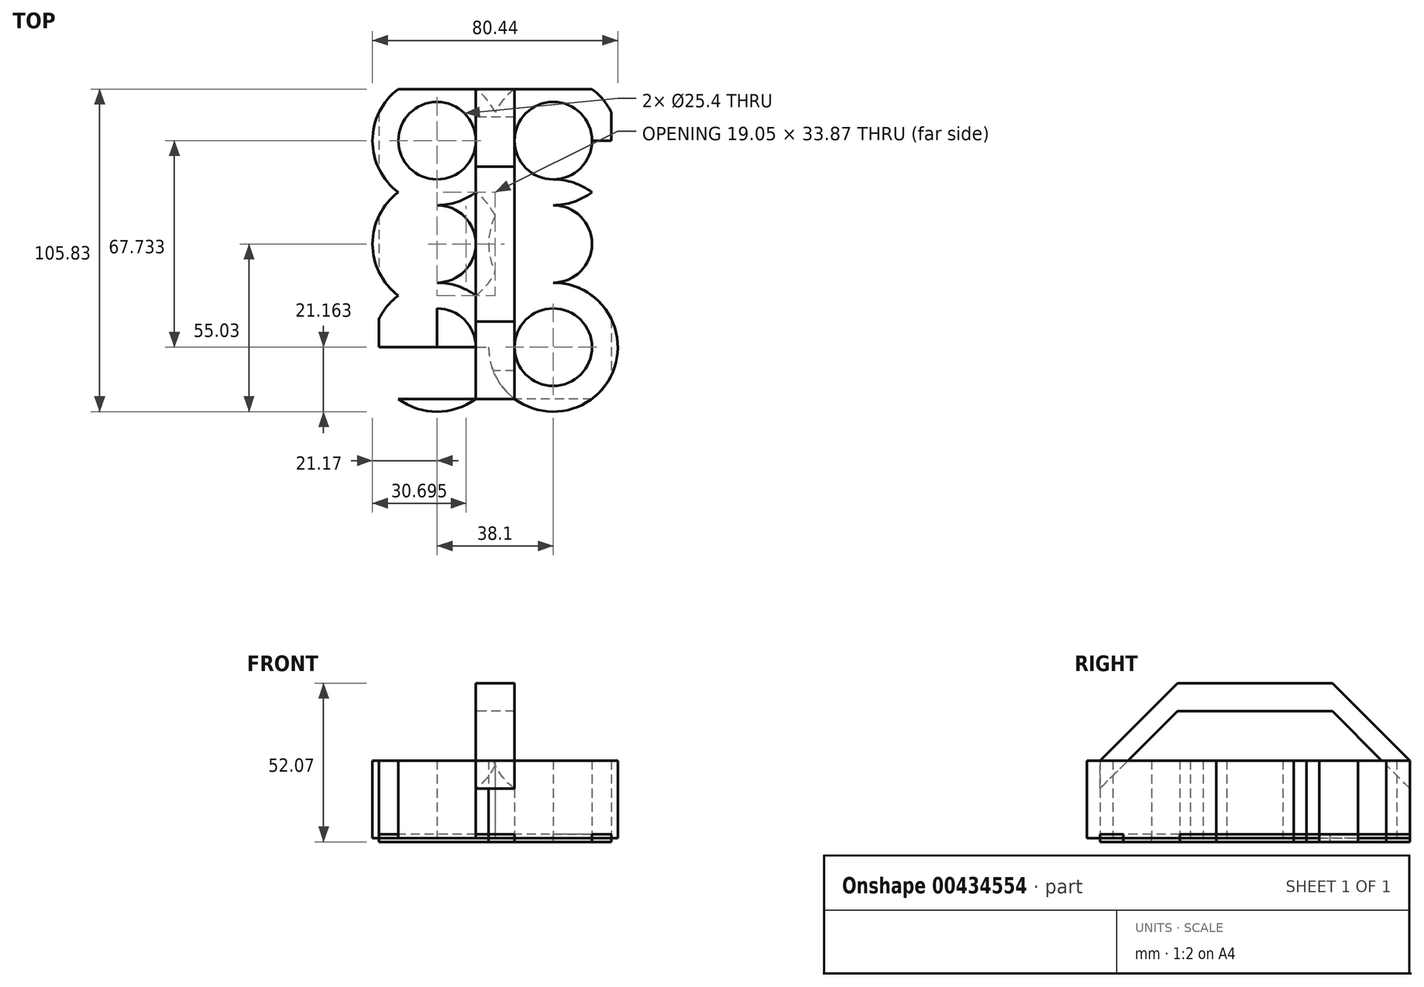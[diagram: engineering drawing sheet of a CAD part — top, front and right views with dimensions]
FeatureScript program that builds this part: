
annotation { "Feature Type Name" : "Feature", "Feature Type Description" : "" }
export const myFeature = defineFeature(function(context is Context, id is Id, definition is map)
    precondition{}
    {
        {
            var Q0;
            Q0=qCreatedBy(makeId("Top.planeOp"),FACE);
            var sketch = newSketch(context, id + "F0", { "sketchPlane" : qUnion([Q0])});
            skCircle(sketch, "E0", {"center": v(-19.05, 33.87) * mm, "radius": 12.7 * mm});
            skCircle(sketch, "E1", {"center": v(19.05, 33.87) * mm, "radius": 12.7 * mm});
            skCircle(sketch, "E2", {"center": v(-19.05, 0) * mm, "radius": 12.7 * mm});
            skCircle(sketch, "E3", {"center": v(19.05, 0) * mm, "radius": 12.7 * mm});
            skCircle(sketch, "E4", {"center": v(-19.05, -33.87) * mm, "radius": 12.7 * mm});
            skCircle(sketch, "E5", {"center": v(19.05, -33.87) * mm, "radius": 12.7 * mm});
            skLineSegment(sketch, "E6.bottom", {"start": v(38.1, 50.8) * mm, "end": v(-38.1, 50.8) * mm});
            skLineSegment(sketch, "E6.top", {"start": v(38.1, -50.8) * mm, "end": v(-38.1, -50.8) * mm});
            skLineSegment(sketch, "E6.left", {"start": v(38.1, 50.8) * mm, "end": v(38.1, -50.8) * mm});
            skLineSegment(sketch, "E6.right", {"start": v(-38.1, 50.8) * mm, "end": v(-38.1, -50.8) * mm});
            skPoint(sketch, "E6.middle", {"position": v(0, 0) * mm});
            skLineSegment(sketch, "E7", {"start": v(0, 50.8) * mm, "end": v(0, -50.8) * mm});
            skLineSegment(sketch, "E8", {"start": v(-38.1, 0) * mm, "end": v(38.1, 0) * mm});
            skLineSegment(sketch, "E9", {"start": v(0, 50.8) * mm, "end": v(-38.1, 50.8) * mm});
            skLineSegment(sketch, "E10", {"start": v(-19.05, 50.8) * mm, "end": v(-19.05, -50.8) * mm});
            skLineSegment(sketch, "E11", {"start": v(0, 50.8) * mm, "end": v(38.1, 50.8) * mm});
            skLineSegment(sketch, "E12", {"start": v(19.05, 50.8) * mm, "end": v(19.05, -50.8) * mm});
            skLineSegment(sketch, "E13", {"start": v(38.1, 50.8) * mm, "end": v(38.1, 16.93) * mm});
            skLineSegment(sketch, "E14", {"start": v(38.1, 16.93) * mm, "end": v(38.1, -16.93) * mm});
            skLineSegment(sketch, "E15", {"start": v(38.1, 16.93) * mm, "end": v(-38.1, 16.93) * mm});
            skLineSegment(sketch, "E16", {"start": v(38.1, -16.93) * mm, "end": v(-38.1, -16.93) * mm});
            skLineSegment(sketch, "E17", {"start": v(-38.1, -16.93) * mm, "end": v(-38.1, -50.8) * mm});
            skLineSegment(sketch, "E18", {"start": v(-38.1, -33.87) * mm, "end": v(38.1, -33.87) * mm});
            skLineSegment(sketch, "E19", {"start": v(38.1, 33.87) * mm, "end": v(-38.1, 33.87) * mm});
            skCircle(sketch, "E20", {"center": v(-19.05, 0) * mm, "radius": 21.17 * mm});
            skCircle(sketch, "E21", {"center": v(19.05, 0) * mm, "radius": 21.17 * mm});
            skCircle(sketch, "E22", {"center": v(-19.05, 33.87) * mm, "radius": 21.17 * mm});
            skCircle(sketch, "E23", {"center": v(19.05, 33.87) * mm, "radius": 21.17 * mm});
            skCircle(sketch, "E24", {"center": v(19.05, -33.87) * mm, "radius": 21.17 * mm});
            skCircle(sketch, "E25", {"center": v(-19.05, -33.87) * mm, "radius": 21.17 * mm});
            skSolve(sketch);
        }
        {
            var Q0;
            {var subQ1=sQuery(id+"F0.wireOp",EDGE,"E0");var subQ5=sQuery(id+"F0.wireOp",EDGE,"E10");var subQ10=makeQuery(id+"F0.imprint","INTERSECT",VERTEX,{"derivedFrom":[subQ1,subQ5]});Q0=makeQuery(id+"F0.imprint","IMPRINT",FACE,{"disambiguationData":[TD([[makeQuery(id+"F0.imprint","IMPRINT",EDGE,{"disambiguationData":[TD([[subQ10,1.0]])],"derivedFrom":subQ1}),-1.0]])]});}
            var Q1;
            {var subQ0=sQuery(id+"F0.wireOp",EDGE,"E9");var subQ1=makeQuery(id+"F0.imprint","INTERSECT",VERTEX,{"derivedFrom":[subQ0,sQuery(id+"F0.wireOp",EDGE,"E10")]});Q1=makeQuery(id+"F0.imprint","IMPRINT",FACE,{"disambiguationData":[TD([[makeQuery(id+"F0.imprint","IMPRINT",EDGE,{"disambiguationData":[TD([[subQ1,1.0]])],"derivedFrom":subQ0}),-1.0]])]});}
            var Q2;
            {var subQ0=sQuery(id+"F0.wireOp",EDGE,"E10");var subQ3=sQuery(id+"F0.wireOp",EDGE,"E0");var subQ4=makeQuery(id+"F0.imprint","INTERSECT",VERTEX,{"derivedFrom":[subQ3,subQ0]});Q2=makeQuery(id+"F0.imprint","IMPRINT",FACE,{"disambiguationData":[TD([[makeQuery(id+"F0.imprint","IMPRINT",EDGE,{"disambiguationData":[TD([[subQ4,-1.0]])],"derivedFrom":subQ3}),-1.0]])]});}
            var Q3;
            {var subQ0=sQuery(id+"F0.wireOp",EDGE,"E6.right");var subQ1=makeQuery(id+"F0.imprint","INTERSECT",VERTEX,{"derivedFrom":[subQ0,sQuery(id+"F0.wireOp",EDGE,"E19")]});Q3=makeQuery(id+"F0.imprint","IMPRINT",FACE,{"disambiguationData":[TD([[makeQuery(id+"F0.imprint","IMPRINT",EDGE,{"disambiguationData":[TD([[subQ1,1.0]])],"derivedFrom":subQ0}),-1.0]])]});}
            var Q4;
            {var subQ5=sQuery(id+"F0.wireOp",EDGE,"E19");var subQ6=sQuery(id+"F0.wireOp",EDGE,"E6.right");var subQ7=makeQuery(id+"F0.imprint","INTERSECT",VERTEX,{"derivedFrom":[subQ6,subQ5]});Q4=makeQuery(id+"F0.imprint","IMPRINT",FACE,{"disambiguationData":[TD([[makeQuery(id+"F0.imprint","IMPRINT",EDGE,{"disambiguationData":[TD([[subQ7,-1.0]])],"derivedFrom":subQ6}),1.0]])]});}
            var Q5;
            {var subQ0=sQuery(id+"F0.wireOp",EDGE,"E15");var subQ1=sQuery(id+"F0.wireOp",EDGE,"E10");var subQ2=makeQuery(id+"F0.imprint","INTERSECT",VERTEX,{"derivedFrom":[subQ1,subQ0]});Q5=makeQuery(id+"F0.imprint","IMPRINT",FACE,{"disambiguationData":[TD([[makeQuery(id+"F0.imprint","IMPRINT",EDGE,{"disambiguationData":[TD([[subQ2,-1.0]])],"derivedFrom":subQ1}),-1.0]])]});}
            var Q6;
            {var subQ0=sQuery(id+"F0.wireOp",EDGE,"E15");var subQ1=sQuery(id+"F0.wireOp",EDGE,"E10");var subQ2=makeQuery(id+"F0.imprint","INTERSECT",VERTEX,{"derivedFrom":[subQ1,subQ0]});Q6=makeQuery(id+"F0.imprint","IMPRINT",FACE,{"disambiguationData":[TD([[makeQuery(id+"F0.imprint","IMPRINT",EDGE,{"disambiguationData":[TD([[subQ2,1.0]])],"derivedFrom":subQ1}),-1.0]])]});}
            var Q7;
            {var subQ0=sQuery(id+"F0.wireOp",EDGE,"E15");var subQ1=sQuery(id+"F0.wireOp",EDGE,"E10");var subQ2=makeQuery(id+"F0.imprint","INTERSECT",VERTEX,{"derivedFrom":[subQ1,subQ0]});Q7=makeQuery(id+"F0.imprint","IMPRINT",FACE,{"disambiguationData":[TD([[makeQuery(id+"F0.imprint","IMPRINT",EDGE,{"disambiguationData":[TD([[subQ2,1.0]])],"derivedFrom":subQ1}),1.0]])]});}
            var Q8;
            {var subQ0=sQuery(id+"F0.wireOp",EDGE,"E15");var subQ1=sQuery(id+"F0.wireOp",EDGE,"E10");var subQ2=makeQuery(id+"F0.imprint","INTERSECT",VERTEX,{"derivedFrom":[subQ1,subQ0]});Q8=makeQuery(id+"F0.imprint","IMPRINT",FACE,{"disambiguationData":[TD([[makeQuery(id+"F0.imprint","IMPRINT",EDGE,{"disambiguationData":[TD([[subQ2,-1.0]])],"derivedFrom":subQ1}),1.0]])]});}
            var Q9;
            {var subQ5=sQuery(id+"F0.wireOp",EDGE,"E19");var subQ6=sQuery(id+"F0.wireOp",EDGE,"E0");var subQ7=makeQuery(id+"F0.imprint","INTERSECT",VERTEX,{"disambiguationData":[OD(0.0)],"derivedFrom":[subQ6,subQ5]});Q9=makeQuery(id+"F0.imprint","IMPRINT",FACE,{"disambiguationData":[TD([[makeQuery(id+"F0.imprint","IMPRINT",EDGE,{"disambiguationData":[TD([[subQ7,1.0]])],"derivedFrom":subQ5}),1.0]])]});}
            var Q10;
            {var subQ0=sQuery(id+"F0.wireOp",EDGE,"E19");var subQ1=sQuery(id+"F0.wireOp",EDGE,"E7");var subQ2=makeQuery(id+"F0.imprint","INTERSECT",VERTEX,{"derivedFrom":[subQ1,subQ0]});Q10=makeQuery(id+"F0.imprint","IMPRINT",FACE,{"disambiguationData":[TD([[makeQuery(id+"F0.imprint","IMPRINT",EDGE,{"disambiguationData":[TD([[subQ2,-1.0]])],"derivedFrom":subQ0}),1.0]])]});}
            var Q11;
            {var subQ0=sQuery(id+"F0.wireOp",EDGE,"E19");var subQ1=sQuery(id+"F0.wireOp",EDGE,"E7");var subQ2=makeQuery(id+"F0.imprint","INTERSECT",VERTEX,{"derivedFrom":[subQ1,subQ0]});Q11=makeQuery(id+"F0.imprint","IMPRINT",FACE,{"disambiguationData":[TD([[makeQuery(id+"F0.imprint","IMPRINT",EDGE,{"disambiguationData":[TD([[subQ2,1.0]])],"derivedFrom":subQ0}),1.0]])]});}
            var Q12;
            {var subQ0=sQuery(id+"F0.wireOp",EDGE,"E19");var subQ1=sQuery(id+"F0.wireOp",EDGE,"E7");var subQ2=makeQuery(id+"F0.imprint","INTERSECT",VERTEX,{"derivedFrom":[subQ1,subQ0]});Q12=makeQuery(id+"F0.imprint","IMPRINT",FACE,{"disambiguationData":[TD([[makeQuery(id+"F0.imprint","IMPRINT",EDGE,{"disambiguationData":[TD([[subQ2,1.0]])],"derivedFrom":subQ0}),-1.0]])]});}
            var Q13;
            {var subQ0=sQuery(id+"F0.wireOp",EDGE,"E19");var subQ1=sQuery(id+"F0.wireOp",EDGE,"E7");var subQ2=makeQuery(id+"F0.imprint","INTERSECT",VERTEX,{"derivedFrom":[subQ1,subQ0]});Q13=makeQuery(id+"F0.imprint","IMPRINT",FACE,{"disambiguationData":[TD([[makeQuery(id+"F0.imprint","IMPRINT",EDGE,{"disambiguationData":[TD([[subQ2,-1.0]])],"derivedFrom":subQ0}),-1.0]])]});}
            var Q14;
            {var subQ1=sQuery(id+"F0.wireOp",EDGE,"E1");var subQ5=sQuery(id+"F0.wireOp",EDGE,"E12");var subQ8=makeQuery(id+"F0.imprint","INTERSECT",VERTEX,{"derivedFrom":[subQ1,subQ5]});Q14=makeQuery(id+"F0.imprint","IMPRINT",FACE,{"disambiguationData":[TD([[makeQuery(id+"F0.imprint","IMPRINT",EDGE,{"disambiguationData":[TD([[subQ8,-1.0]])],"derivedFrom":subQ1}),-1.0]])]});}
            var Q15;
            {var subQ1=sQuery(id+"F0.wireOp",EDGE,"E19");var subQ6=sQuery(id+"F0.wireOp",EDGE,"E1");var subQ9=makeQuery(id+"F0.imprint","INTERSECT",VERTEX,{"disambiguationData":[OD(1.0)],"derivedFrom":[subQ6,subQ1]});Q15=makeQuery(id+"F0.imprint","IMPRINT",FACE,{"disambiguationData":[TD([[makeQuery(id+"F0.imprint","IMPRINT",EDGE,{"disambiguationData":[TD([[subQ9,-1.0]])],"derivedFrom":subQ1}),1.0]])]});}
            var Q16;
            {var subQ0=sQuery(id+"F0.wireOp",EDGE,"E15");var subQ1=sQuery(id+"F0.wireOp",EDGE,"E12");var subQ2=makeQuery(id+"F0.imprint","INTERSECT",VERTEX,{"derivedFrom":[subQ1,subQ0]});Q16=makeQuery(id+"F0.imprint","IMPRINT",FACE,{"disambiguationData":[TD([[makeQuery(id+"F0.imprint","IMPRINT",EDGE,{"disambiguationData":[TD([[subQ2,-1.0]])],"derivedFrom":subQ1}),-1.0]])]});}
            var Q17;
            {var subQ0=sQuery(id+"F0.wireOp",EDGE,"E15");var subQ1=sQuery(id+"F0.wireOp",EDGE,"E12");var subQ2=makeQuery(id+"F0.imprint","INTERSECT",VERTEX,{"derivedFrom":[subQ1,subQ0]});Q17=makeQuery(id+"F0.imprint","IMPRINT",FACE,{"disambiguationData":[TD([[makeQuery(id+"F0.imprint","IMPRINT",EDGE,{"disambiguationData":[TD([[subQ2,1.0]])],"derivedFrom":subQ1}),-1.0]])]});}
            var Q18;
            {var subQ0=sQuery(id+"F0.wireOp",EDGE,"E15");var subQ1=sQuery(id+"F0.wireOp",EDGE,"E12");var subQ2=makeQuery(id+"F0.imprint","INTERSECT",VERTEX,{"derivedFrom":[subQ1,subQ0]});Q18=makeQuery(id+"F0.imprint","IMPRINT",FACE,{"disambiguationData":[TD([[makeQuery(id+"F0.imprint","IMPRINT",EDGE,{"disambiguationData":[TD([[subQ2,-1.0]])],"derivedFrom":subQ1}),1.0]])]});}
            var Q19;
            {var subQ0=sQuery(id+"F0.wireOp",EDGE,"E15");var subQ1=sQuery(id+"F0.wireOp",EDGE,"E12");var subQ2=makeQuery(id+"F0.imprint","INTERSECT",VERTEX,{"derivedFrom":[subQ1,subQ0]});Q19=makeQuery(id+"F0.imprint","IMPRINT",FACE,{"disambiguationData":[TD([[makeQuery(id+"F0.imprint","IMPRINT",EDGE,{"disambiguationData":[TD([[subQ2,1.0]])],"derivedFrom":subQ1}),1.0]])]});}
            var Q20;
            {var subQ5=sQuery(id+"F0.wireOp",EDGE,"E19");var subQ6=sQuery(id+"F0.wireOp",EDGE,"E13");var subQ7=makeQuery(id+"F0.imprint","INTERSECT",VERTEX,{"derivedFrom":[subQ6,subQ5]});Q20=makeQuery(id+"F0.imprint","IMPRINT",FACE,{"disambiguationData":[TD([[makeQuery(id+"F0.imprint","IMPRINT",EDGE,{"disambiguationData":[TD([[subQ7,-1.0]])],"derivedFrom":subQ6}),-1.0]])]});}
            var Q21;
            {var subQ0=sQuery(id+"F0.wireOp",EDGE,"E12");var subQ3=sQuery(id+"F0.wireOp",EDGE,"E1");var subQ4=makeQuery(id+"F0.imprint","INTERSECT",VERTEX,{"derivedFrom":[subQ3,subQ0]});Q21=makeQuery(id+"F0.imprint","IMPRINT",FACE,{"disambiguationData":[TD([[makeQuery(id+"F0.imprint","IMPRINT",EDGE,{"disambiguationData":[TD([[subQ4,1.0]])],"derivedFrom":subQ3}),-1.0]])]});}
            var Q22;
            {var subQ0=sQuery(id+"F0.wireOp",EDGE,"E11");var subQ1=makeQuery(id+"F0.imprint","INTERSECT",VERTEX,{"derivedFrom":[subQ0,sQuery(id+"F0.wireOp",EDGE,"E12")]});Q22=makeQuery(id+"F0.imprint","IMPRINT",FACE,{"disambiguationData":[TD([[makeQuery(id+"F0.imprint","IMPRINT",EDGE,{"disambiguationData":[TD([[subQ1,1.0]])],"derivedFrom":subQ0}),1.0]])]});}
            var Q23;
            {var subQ0=sQuery(id+"F0.wireOp",EDGE,"E13");var subQ1=makeQuery(id+"F0.imprint","INTERSECT",VERTEX,{"derivedFrom":[subQ0,sQuery(id+"F0.wireOp",EDGE,"E19")]});Q23=makeQuery(id+"F0.imprint","IMPRINT",FACE,{"disambiguationData":[TD([[makeQuery(id+"F0.imprint","IMPRINT",EDGE,{"disambiguationData":[TD([[subQ1,1.0]])],"derivedFrom":subQ0}),1.0]])]});}
            var Q24;
            {var subQ0=sQuery(id+"F0.wireOp",EDGE,"E8");var subQ1=sQuery(id+"F0.wireOp",EDGE,"E7");var subQ2=makeQuery(id+"F0.imprint","INTERSECT",VERTEX,{"derivedFrom":[subQ1,subQ0]});Q24=makeQuery(id+"F0.imprint","IMPRINT",FACE,{"disambiguationData":[TD([[makeQuery(id+"F0.imprint","IMPRINT",EDGE,{"disambiguationData":[TD([[subQ2,-1.0]])],"derivedFrom":subQ0}),1.0]])]});}
            var Q25;
            {var subQ0=sQuery(id+"F0.wireOp",EDGE,"E8");var subQ1=sQuery(id+"F0.wireOp",EDGE,"E7");var subQ2=makeQuery(id+"F0.imprint","INTERSECT",VERTEX,{"derivedFrom":[subQ1,subQ0]});Q25=makeQuery(id+"F0.imprint","IMPRINT",FACE,{"disambiguationData":[TD([[makeQuery(id+"F0.imprint","IMPRINT",EDGE,{"disambiguationData":[TD([[subQ2,1.0]])],"derivedFrom":subQ0}),1.0]])]});}
            var Q26;
            {var subQ0=sQuery(id+"F0.wireOp",EDGE,"E8");var subQ1=sQuery(id+"F0.wireOp",EDGE,"E7");var subQ2=makeQuery(id+"F0.imprint","INTERSECT",VERTEX,{"derivedFrom":[subQ1,subQ0]});Q26=makeQuery(id+"F0.imprint","IMPRINT",FACE,{"disambiguationData":[TD([[makeQuery(id+"F0.imprint","IMPRINT",EDGE,{"disambiguationData":[TD([[subQ2,1.0]])],"derivedFrom":subQ0}),-1.0]])]});}
            var Q27;
            {var subQ0=sQuery(id+"F0.wireOp",EDGE,"E8");var subQ1=sQuery(id+"F0.wireOp",EDGE,"E7");var subQ2=makeQuery(id+"F0.imprint","INTERSECT",VERTEX,{"derivedFrom":[subQ1,subQ0]});Q27=makeQuery(id+"F0.imprint","IMPRINT",FACE,{"disambiguationData":[TD([[makeQuery(id+"F0.imprint","IMPRINT",EDGE,{"disambiguationData":[TD([[subQ2,-1.0]])],"derivedFrom":subQ0}),-1.0]])]});}
            var Q28;
            {var subQ1=sQuery(id+"F0.wireOp",EDGE,"E8");var subQ7=sQuery(id+"F0.wireOp",EDGE,"E2");var subQ8=makeQuery(id+"F0.imprint","INTERSECT",VERTEX,{"disambiguationData":[OD(0.0)],"derivedFrom":[subQ7,subQ1]});Q28=makeQuery(id+"F0.imprint","IMPRINT",FACE,{"disambiguationData":[TD([[makeQuery(id+"F0.imprint","IMPRINT",EDGE,{"disambiguationData":[TD([[subQ8,-1.0]])],"derivedFrom":subQ1}),1.0]])]});}
            var Q29;
            {var subQ1=sQuery(id+"F0.wireOp",EDGE,"E8");var subQ7=sQuery(id+"F0.wireOp",EDGE,"E2");var subQ8=makeQuery(id+"F0.imprint","INTERSECT",VERTEX,{"disambiguationData":[OD(0.0)],"derivedFrom":[subQ7,subQ1]});Q29=makeQuery(id+"F0.imprint","IMPRINT",FACE,{"disambiguationData":[TD([[makeQuery(id+"F0.imprint","IMPRINT",EDGE,{"disambiguationData":[TD([[subQ8,-1.0]])],"derivedFrom":subQ1}),-1.0]])]});}
            var Q30;
            {var subQ0=sQuery(id+"F0.wireOp",EDGE,"E16");var subQ1=sQuery(id+"F0.wireOp",EDGE,"E10");var subQ2=makeQuery(id+"F0.imprint","INTERSECT",VERTEX,{"derivedFrom":[subQ1,subQ0]});Q30=makeQuery(id+"F0.imprint","IMPRINT",FACE,{"disambiguationData":[TD([[makeQuery(id+"F0.imprint","IMPRINT",EDGE,{"disambiguationData":[TD([[subQ2,1.0]])],"derivedFrom":subQ1}),1.0]])]});}
            var Q31;
            {var subQ0=sQuery(id+"F0.wireOp",EDGE,"E16");var subQ1=sQuery(id+"F0.wireOp",EDGE,"E10");var subQ2=makeQuery(id+"F0.imprint","INTERSECT",VERTEX,{"derivedFrom":[subQ1,subQ0]});Q31=makeQuery(id+"F0.imprint","IMPRINT",FACE,{"disambiguationData":[TD([[makeQuery(id+"F0.imprint","IMPRINT",EDGE,{"disambiguationData":[TD([[subQ2,-1.0]])],"derivedFrom":subQ1}),1.0]])]});}
            var Q32;
            {var subQ0=sQuery(id+"F0.wireOp",EDGE,"E16");var subQ1=sQuery(id+"F0.wireOp",EDGE,"E10");var subQ2=makeQuery(id+"F0.imprint","INTERSECT",VERTEX,{"derivedFrom":[subQ1,subQ0]});Q32=makeQuery(id+"F0.imprint","IMPRINT",FACE,{"disambiguationData":[TD([[makeQuery(id+"F0.imprint","IMPRINT",EDGE,{"disambiguationData":[TD([[subQ2,-1.0]])],"derivedFrom":subQ1}),-1.0]])]});}
            var Q33;
            {var subQ0=sQuery(id+"F0.wireOp",EDGE,"E16");var subQ1=sQuery(id+"F0.wireOp",EDGE,"E10");var subQ2=makeQuery(id+"F0.imprint","INTERSECT",VERTEX,{"derivedFrom":[subQ1,subQ0]});Q33=makeQuery(id+"F0.imprint","IMPRINT",FACE,{"disambiguationData":[TD([[makeQuery(id+"F0.imprint","IMPRINT",EDGE,{"disambiguationData":[TD([[subQ2,1.0]])],"derivedFrom":subQ1}),-1.0]])]});}
            var Q34;
            {var subQ0=sQuery(id+"F0.wireOp",EDGE,"E8");var subQ1=sQuery(id+"F0.wireOp",EDGE,"E6.right");var subQ2=makeQuery(id+"F0.imprint","INTERSECT",VERTEX,{"derivedFrom":[subQ1,subQ0]});Q34=makeQuery(id+"F0.imprint","IMPRINT",FACE,{"disambiguationData":[TD([[makeQuery(id+"F0.imprint","IMPRINT",EDGE,{"disambiguationData":[TD([[subQ2,-1.0]])],"derivedFrom":subQ1}),1.0]])]});}
            var Q35;
            {var subQ0=sQuery(id+"F0.wireOp",EDGE,"E6.right");var subQ1=makeQuery(id+"F0.imprint","INTERSECT",VERTEX,{"derivedFrom":[subQ0,sQuery(id+"F0.wireOp",EDGE,"E8")]});Q35=makeQuery(id+"F0.imprint","IMPRINT",FACE,{"disambiguationData":[TD([[makeQuery(id+"F0.imprint","IMPRINT",EDGE,{"disambiguationData":[TD([[subQ1,1.0]])],"derivedFrom":subQ0}),-1.0]])]});}
            var Q36;
            {var subQ1=sQuery(id+"F0.wireOp",EDGE,"E6.right");var subQ5=sQuery(id+"F0.wireOp",EDGE,"E8");var subQ6=makeQuery(id+"F0.imprint","INTERSECT",VERTEX,{"derivedFrom":[subQ1,subQ5]});Q36=makeQuery(id+"F0.imprint","IMPRINT",FACE,{"disambiguationData":[TD([[makeQuery(id+"F0.imprint","IMPRINT",EDGE,{"disambiguationData":[TD([[subQ6,1.0]])],"derivedFrom":subQ1}),1.0]])]});}
            var Q37;
            {var subQ5=sQuery(id+"F0.wireOp",EDGE,"E8");var subQ7=sQuery(id+"F0.wireOp",EDGE,"E3");var subQ8=makeQuery(id+"F0.imprint","INTERSECT",VERTEX,{"disambiguationData":[OD(1.0)],"derivedFrom":[subQ7,subQ5]});Q37=makeQuery(id+"F0.imprint","IMPRINT",FACE,{"disambiguationData":[TD([[makeQuery(id+"F0.imprint","IMPRINT",EDGE,{"disambiguationData":[TD([[subQ8,1.0]])],"derivedFrom":subQ5}),1.0]])]});}
            var Q38;
            {var subQ0=sQuery(id+"F0.wireOp",EDGE,"E16");var subQ1=sQuery(id+"F0.wireOp",EDGE,"E12");var subQ2=makeQuery(id+"F0.imprint","INTERSECT",VERTEX,{"derivedFrom":[subQ1,subQ0]});Q38=makeQuery(id+"F0.imprint","IMPRINT",FACE,{"disambiguationData":[TD([[makeQuery(id+"F0.imprint","IMPRINT",EDGE,{"disambiguationData":[TD([[subQ2,1.0]])],"derivedFrom":subQ1}),-1.0]])]});}
            var Q39;
            {var subQ0=sQuery(id+"F0.wireOp",EDGE,"E16");var subQ1=sQuery(id+"F0.wireOp",EDGE,"E12");var subQ2=makeQuery(id+"F0.imprint","INTERSECT",VERTEX,{"derivedFrom":[subQ1,subQ0]});Q39=makeQuery(id+"F0.imprint","IMPRINT",FACE,{"disambiguationData":[TD([[makeQuery(id+"F0.imprint","IMPRINT",EDGE,{"disambiguationData":[TD([[subQ2,-1.0]])],"derivedFrom":subQ1}),-1.0]])]});}
            var Q40;
            {var subQ0=sQuery(id+"F0.wireOp",EDGE,"E16");var subQ1=sQuery(id+"F0.wireOp",EDGE,"E12");var subQ2=makeQuery(id+"F0.imprint","INTERSECT",VERTEX,{"derivedFrom":[subQ1,subQ0]});Q40=makeQuery(id+"F0.imprint","IMPRINT",FACE,{"disambiguationData":[TD([[makeQuery(id+"F0.imprint","IMPRINT",EDGE,{"disambiguationData":[TD([[subQ2,-1.0]])],"derivedFrom":subQ1}),1.0]])]});}
            var Q41;
            {var subQ0=sQuery(id+"F0.wireOp",EDGE,"E16");var subQ1=sQuery(id+"F0.wireOp",EDGE,"E12");var subQ2=makeQuery(id+"F0.imprint","INTERSECT",VERTEX,{"derivedFrom":[subQ1,subQ0]});Q41=makeQuery(id+"F0.imprint","IMPRINT",FACE,{"disambiguationData":[TD([[makeQuery(id+"F0.imprint","IMPRINT",EDGE,{"disambiguationData":[TD([[subQ2,1.0]])],"derivedFrom":subQ1}),1.0]])]});}
            var Q42;
            {var subQ1=sQuery(id+"F0.wireOp",EDGE,"E14");var subQ5=sQuery(id+"F0.wireOp",EDGE,"E8");var subQ6=makeQuery(id+"F0.imprint","INTERSECT",VERTEX,{"derivedFrom":[subQ5,subQ1]});Q42=makeQuery(id+"F0.imprint","IMPRINT",FACE,{"disambiguationData":[TD([[makeQuery(id+"F0.imprint","IMPRINT",EDGE,{"disambiguationData":[TD([[subQ6,1.0]])],"derivedFrom":subQ5}),-1.0]])]});}
            var Q43;
            {var subQ0=sQuery(id+"F0.wireOp",EDGE,"E14");var subQ1=sQuery(id+"F0.wireOp",EDGE,"E8");var subQ2=makeQuery(id+"F0.imprint","INTERSECT",VERTEX,{"derivedFrom":[subQ1,subQ0]});Q43=makeQuery(id+"F0.imprint","IMPRINT",FACE,{"disambiguationData":[TD([[makeQuery(id+"F0.imprint","IMPRINT",EDGE,{"disambiguationData":[TD([[subQ2,1.0]])],"derivedFrom":subQ1}),1.0]])]});}
            var Q44;
            {var subQ0=sQuery(id+"F0.wireOp",EDGE,"E14");var subQ1=makeQuery(id+"F0.imprint","INTERSECT",VERTEX,{"derivedFrom":[sQuery(id+"F0.wireOp",EDGE,"E8"),subQ0]});Q44=makeQuery(id+"F0.imprint","IMPRINT",FACE,{"disambiguationData":[TD([[makeQuery(id+"F0.imprint","IMPRINT",EDGE,{"disambiguationData":[TD([[subQ1,1.0]])],"derivedFrom":subQ0}),1.0]])]});}
            var Q45;
            {var subQ5=sQuery(id+"F0.wireOp",EDGE,"E8");var subQ7=sQuery(id+"F0.wireOp",EDGE,"E3");var subQ8=makeQuery(id+"F0.imprint","INTERSECT",VERTEX,{"disambiguationData":[OD(1.0)],"derivedFrom":[subQ7,subQ5]});Q45=makeQuery(id+"F0.imprint","IMPRINT",FACE,{"disambiguationData":[TD([[makeQuery(id+"F0.imprint","IMPRINT",EDGE,{"disambiguationData":[TD([[subQ8,1.0]])],"derivedFrom":subQ5}),-1.0]])]});}
            var Q46;
            {var subQ1=sQuery(id+"F0.wireOp",EDGE,"E5");var subQ5=sQuery(id+"F0.wireOp",EDGE,"E18");var subQ6=makeQuery(id+"F0.imprint","INTERSECT",VERTEX,{"disambiguationData":[OD(1.0)],"derivedFrom":[subQ1,subQ5]});Q46=makeQuery(id+"F0.imprint","IMPRINT",FACE,{"disambiguationData":[TD([[makeQuery(id+"F0.imprint","IMPRINT",EDGE,{"disambiguationData":[TD([[subQ6,1.0]])],"derivedFrom":subQ5}),1.0]])]});}
            var Q47;
            {var subQ0=sQuery(id+"F0.wireOp",EDGE,"E18");var subQ1=sQuery(id+"F0.wireOp",EDGE,"E7");var subQ2=makeQuery(id+"F0.imprint","INTERSECT",VERTEX,{"derivedFrom":[subQ1,subQ0]});Q47=makeQuery(id+"F0.imprint","IMPRINT",FACE,{"disambiguationData":[TD([[makeQuery(id+"F0.imprint","IMPRINT",EDGE,{"disambiguationData":[TD([[subQ2,-1.0]])],"derivedFrom":subQ0}),1.0]])]});}
            var Q48;
            {var subQ0=sQuery(id+"F0.wireOp",EDGE,"E18");var subQ1=sQuery(id+"F0.wireOp",EDGE,"E7");var subQ2=makeQuery(id+"F0.imprint","INTERSECT",VERTEX,{"derivedFrom":[subQ1,subQ0]});Q48=makeQuery(id+"F0.imprint","IMPRINT",FACE,{"disambiguationData":[TD([[makeQuery(id+"F0.imprint","IMPRINT",EDGE,{"disambiguationData":[TD([[subQ2,1.0]])],"derivedFrom":subQ0}),1.0]])]});}
            var Q49;
            {var subQ0=sQuery(id+"F0.wireOp",EDGE,"E18");var subQ1=sQuery(id+"F0.wireOp",EDGE,"E7");var subQ2=makeQuery(id+"F0.imprint","INTERSECT",VERTEX,{"derivedFrom":[subQ1,subQ0]});Q49=makeQuery(id+"F0.imprint","IMPRINT",FACE,{"disambiguationData":[TD([[makeQuery(id+"F0.imprint","IMPRINT",EDGE,{"disambiguationData":[TD([[subQ2,-1.0]])],"derivedFrom":subQ0}),-1.0]])]});}
            var Q50;
            {var subQ0=sQuery(id+"F0.wireOp",EDGE,"E18");var subQ1=sQuery(id+"F0.wireOp",EDGE,"E7");var subQ2=makeQuery(id+"F0.imprint","INTERSECT",VERTEX,{"derivedFrom":[subQ1,subQ0]});Q50=makeQuery(id+"F0.imprint","IMPRINT",FACE,{"disambiguationData":[TD([[makeQuery(id+"F0.imprint","IMPRINT",EDGE,{"disambiguationData":[TD([[subQ2,1.0]])],"derivedFrom":subQ0}),-1.0]])]});}
            var Q51;
            {var subQ5=sQuery(id+"F0.wireOp",EDGE,"E18");var subQ6=sQuery(id+"F0.wireOp",EDGE,"E5");var subQ7=makeQuery(id+"F0.imprint","INTERSECT",VERTEX,{"disambiguationData":[OD(1.0)],"derivedFrom":[subQ6,subQ5]});Q51=makeQuery(id+"F0.imprint","IMPRINT",FACE,{"disambiguationData":[TD([[makeQuery(id+"F0.imprint","IMPRINT",EDGE,{"disambiguationData":[TD([[subQ7,-1.0]])],"derivedFrom":subQ6}),-1.0]])]});}
            var Q52;
            {var subQ0=sQuery(id+"F0.wireOp",EDGE,"E6.top");var subQ1=makeQuery(id+"F0.imprint","INTERSECT",VERTEX,{"derivedFrom":[subQ0,sQuery(id+"F0.wireOp",EDGE,"E12")]});Q52=makeQuery(id+"F0.imprint","IMPRINT",FACE,{"disambiguationData":[TD([[makeQuery(id+"F0.imprint","IMPRINT",EDGE,{"disambiguationData":[TD([[subQ1,1.0]])],"derivedFrom":subQ0}),1.0]])]});}
            var Q53;
            {var subQ3=sQuery(id+"F0.wireOp",EDGE,"E5");var subQ9=sQuery(id+"F0.wireOp",EDGE,"E18");var subQ11=makeQuery(id+"F0.imprint","INTERSECT",VERTEX,{"disambiguationData":[OD(0.0)],"derivedFrom":[subQ3,subQ9]});Q53=makeQuery(id+"F0.imprint","IMPRINT",FACE,{"disambiguationData":[TD([[makeQuery(id+"F0.imprint","IMPRINT",EDGE,{"disambiguationData":[TD([[subQ11,1.0]])],"derivedFrom":subQ3}),-1.0]])]});}
            var Q54;
            {var subQ0=sQuery(id+"F0.wireOp",EDGE,"E18");var subQ1=sQuery(id+"F0.wireOp",EDGE,"E6.left");var subQ2=makeQuery(id+"F0.imprint","INTERSECT",VERTEX,{"derivedFrom":[subQ1,subQ0]});Q54=makeQuery(id+"F0.imprint","IMPRINT",FACE,{"disambiguationData":[TD([[makeQuery(id+"F0.imprint","IMPRINT",EDGE,{"disambiguationData":[TD([[subQ2,1.0]])],"derivedFrom":subQ1}),-1.0]])]});}
            var Q55;
            {var subQ0=sQuery(id+"F0.wireOp",EDGE,"E6.left");var subQ1=makeQuery(id+"F0.imprint","INTERSECT",VERTEX,{"derivedFrom":[subQ0,sQuery(id+"F0.wireOp",EDGE,"E18")]});Q55=makeQuery(id+"F0.imprint","IMPRINT",FACE,{"disambiguationData":[TD([[makeQuery(id+"F0.imprint","IMPRINT",EDGE,{"disambiguationData":[TD([[subQ1,1.0]])],"derivedFrom":subQ0}),1.0]])]});}
            var Q56;
            {var subQ1=sQuery(id+"F0.wireOp",EDGE,"E18");var subQ5=sQuery(id+"F0.wireOp",EDGE,"E4");var subQ6=makeQuery(id+"F0.imprint","INTERSECT",VERTEX,{"disambiguationData":[OD(0.0)],"derivedFrom":[subQ5,subQ1]});Q56=makeQuery(id+"F0.imprint","IMPRINT",FACE,{"disambiguationData":[TD([[makeQuery(id+"F0.imprint","IMPRINT",EDGE,{"disambiguationData":[TD([[subQ6,-1.0]])],"derivedFrom":subQ1}),1.0]])]});}
            var Q57;
            {var subQ0=sQuery(id+"F0.wireOp",EDGE,"E18");var subQ1=sQuery(id+"F0.wireOp",EDGE,"E17");var subQ2=makeQuery(id+"F0.imprint","INTERSECT",VERTEX,{"derivedFrom":[subQ1,subQ0]});Q57=makeQuery(id+"F0.imprint","IMPRINT",FACE,{"disambiguationData":[TD([[makeQuery(id+"F0.imprint","IMPRINT",EDGE,{"disambiguationData":[TD([[subQ2,1.0]])],"derivedFrom":subQ1}),1.0]])]});}
            var Q58;
            {var subQ0=sQuery(id+"F0.wireOp",EDGE,"E17");var subQ1=makeQuery(id+"F0.imprint","INTERSECT",VERTEX,{"derivedFrom":[subQ0,sQuery(id+"F0.wireOp",EDGE,"E18")]});Q58=makeQuery(id+"F0.imprint","IMPRINT",FACE,{"disambiguationData":[TD([[makeQuery(id+"F0.imprint","IMPRINT",EDGE,{"disambiguationData":[TD([[subQ1,1.0]])],"derivedFrom":subQ0}),-1.0]])]});}
            var Q59;
            {var subQ0=sQuery(id+"F0.wireOp",EDGE,"E18");var subQ8=sQuery(id+"F0.wireOp",EDGE,"E4");var subQ11=makeQuery(id+"F0.imprint","INTERSECT",VERTEX,{"disambiguationData":[OD(1.0)],"derivedFrom":[subQ8,subQ0]});Q59=makeQuery(id+"F0.imprint","IMPRINT",FACE,{"disambiguationData":[TD([[makeQuery(id+"F0.imprint","IMPRINT",EDGE,{"disambiguationData":[TD([[subQ11,-1.0]])],"derivedFrom":subQ8}),-1.0]])]});}
            var Q60;
            {var subQ0=sQuery(id+"F0.wireOp",EDGE,"E6.top");var subQ1=makeQuery(id+"F0.imprint","INTERSECT",VERTEX,{"derivedFrom":[subQ0,sQuery(id+"F0.wireOp",EDGE,"E10")]});Q60=makeQuery(id+"F0.imprint","IMPRINT",FACE,{"disambiguationData":[TD([[makeQuery(id+"F0.imprint","IMPRINT",EDGE,{"disambiguationData":[TD([[subQ1,1.0]])],"derivedFrom":subQ0}),1.0]])]});}
            var Q61;
            {var subQ3=sQuery(id+"F0.wireOp",EDGE,"E4");var subQ5=sQuery(id+"F0.wireOp",EDGE,"E18");var subQ6=makeQuery(id+"F0.imprint","INTERSECT",VERTEX,{"disambiguationData":[OD(0.0)],"derivedFrom":[subQ3,subQ5]});Q61=makeQuery(id+"F0.imprint","IMPRINT",FACE,{"disambiguationData":[TD([[makeQuery(id+"F0.imprint","IMPRINT",EDGE,{"disambiguationData":[TD([[subQ6,1.0]])],"derivedFrom":subQ3}),-1.0]])]});}
            var Q62;
            {var subQ0=sQuery(id+"F0.wireOp",EDGE,"E15");var subQ1=sQuery(id+"F0.wireOp",EDGE,"E7");var subQ2=makeQuery(id+"F0.imprint","INTERSECT",VERTEX,{"derivedFrom":[subQ1,subQ0]});Q62=makeQuery(id+"F0.imprint","IMPRINT",FACE,{"disambiguationData":[TD([[makeQuery(id+"F0.imprint","IMPRINT",EDGE,{"disambiguationData":[TD([[subQ2,-1.0]])],"derivedFrom":subQ1}),-1.0]])]});}
            var Q63;
            {var subQ0=sQuery(id+"F0.wireOp",EDGE,"E15");var subQ1=sQuery(id+"F0.wireOp",EDGE,"E7");var subQ2=makeQuery(id+"F0.imprint","INTERSECT",VERTEX,{"derivedFrom":[subQ1,subQ0]});Q63=makeQuery(id+"F0.imprint","IMPRINT",FACE,{"disambiguationData":[TD([[makeQuery(id+"F0.imprint","IMPRINT",EDGE,{"disambiguationData":[TD([[subQ2,-1.0]])],"derivedFrom":subQ1}),1.0]])]});}
            var Q64;
            {var subQ0=sQuery(id+"F0.wireOp",EDGE,"E15");var subQ1=sQuery(id+"F0.wireOp",EDGE,"E7");var subQ2=makeQuery(id+"F0.imprint","INTERSECT",VERTEX,{"derivedFrom":[subQ1,subQ0]});Q64=makeQuery(id+"F0.imprint","IMPRINT",FACE,{"disambiguationData":[TD([[makeQuery(id+"F0.imprint","IMPRINT",EDGE,{"disambiguationData":[TD([[subQ2,1.0]])],"derivedFrom":subQ1}),1.0]])]});}
            var Q65;
            {var subQ0=sQuery(id+"F0.wireOp",EDGE,"E15");var subQ1=sQuery(id+"F0.wireOp",EDGE,"E7");var subQ2=makeQuery(id+"F0.imprint","INTERSECT",VERTEX,{"derivedFrom":[subQ1,subQ0]});Q65=makeQuery(id+"F0.imprint","IMPRINT",FACE,{"disambiguationData":[TD([[makeQuery(id+"F0.imprint","IMPRINT",EDGE,{"disambiguationData":[TD([[subQ2,1.0]])],"derivedFrom":subQ1}),-1.0]])]});}
            var Q66;
            {var subQ0=sQuery(id+"F0.wireOp",EDGE,"E16");var subQ1=sQuery(id+"F0.wireOp",EDGE,"E7");var subQ2=makeQuery(id+"F0.imprint","INTERSECT",VERTEX,{"derivedFrom":[subQ1,subQ0]});Q66=makeQuery(id+"F0.imprint","IMPRINT",FACE,{"disambiguationData":[TD([[makeQuery(id+"F0.imprint","IMPRINT",EDGE,{"disambiguationData":[TD([[subQ2,1.0]])],"derivedFrom":subQ1}),-1.0]])]});}
            var Q67;
            {var subQ0=sQuery(id+"F0.wireOp",EDGE,"E16");var subQ1=sQuery(id+"F0.wireOp",EDGE,"E7");var subQ2=makeQuery(id+"F0.imprint","INTERSECT",VERTEX,{"derivedFrom":[subQ1,subQ0]});Q67=makeQuery(id+"F0.imprint","IMPRINT",FACE,{"disambiguationData":[TD([[makeQuery(id+"F0.imprint","IMPRINT",EDGE,{"disambiguationData":[TD([[subQ2,1.0]])],"derivedFrom":subQ1}),1.0]])]});}
            var Q68;
            {var subQ0=sQuery(id+"F0.wireOp",EDGE,"E16");var subQ1=sQuery(id+"F0.wireOp",EDGE,"E7");var subQ2=makeQuery(id+"F0.imprint","INTERSECT",VERTEX,{"derivedFrom":[subQ1,subQ0]});Q68=makeQuery(id+"F0.imprint","IMPRINT",FACE,{"disambiguationData":[TD([[makeQuery(id+"F0.imprint","IMPRINT",EDGE,{"disambiguationData":[TD([[subQ2,-1.0]])],"derivedFrom":subQ1}),1.0]])]});}
            var Q69;
            {var subQ0=sQuery(id+"F0.wireOp",EDGE,"E16");var subQ1=sQuery(id+"F0.wireOp",EDGE,"E7");var subQ2=makeQuery(id+"F0.imprint","INTERSECT",VERTEX,{"derivedFrom":[subQ1,subQ0]});Q69=makeQuery(id+"F0.imprint","IMPRINT",FACE,{"disambiguationData":[TD([[makeQuery(id+"F0.imprint","IMPRINT",EDGE,{"disambiguationData":[TD([[subQ2,-1.0]])],"derivedFrom":subQ1}),-1.0]])]});}
            extrude(context, id + "F1", {"entities" : qUnion([Q0, Q1, Q2, Q3, Q4, Q5, Q6, Q7, Q8, Q9, Q10, Q11, Q12, Q13, Q14, Q15, Q16, Q17, Q18, Q19, Q20, Q21, Q22, Q23, Q24, Q25, Q26, Q27, Q28, Q29, Q30, Q31, Q32, Q33, Q34, Q35, Q36, Q37, Q38, Q39, Q40, Q41, Q42, Q43, Q44, Q45, Q46, Q47, Q48, Q49, Q50, Q51, Q52, Q53, Q54, Q55, Q56, Q57, Q58, Q59, Q60, Q61, Q62, Q63, Q64, Q65, Q66, Q67, Q68, Q69]), "depth" : 25.4 * mm});
        }
        {
            var Q0;
            {var subQ0=sQuery(id+"F0.wireOp",EDGE,"E10");var subQ1=sQuery(id+"F0.wireOp",EDGE,"E0");var subQ2=makeQuery(id+"F0.imprint","INTERSECT",VERTEX,{"derivedFrom":[subQ1,subQ0]});Q0=makeQuery(id+"F0.imprint","IMPRINT",FACE,{"disambiguationData":[TD([[makeQuery(id+"F0.imprint","IMPRINT",EDGE,{"disambiguationData":[TD([[subQ2,-1.0]])],"derivedFrom":subQ1}),1.0]])]});}
            var Q1;
            {var subQ0=sQuery(id+"F0.wireOp",EDGE,"E10");var subQ1=sQuery(id+"F0.wireOp",EDGE,"E0");var subQ2=makeQuery(id+"F0.imprint","INTERSECT",VERTEX,{"derivedFrom":[subQ1,subQ0]});Q1=makeQuery(id+"F0.imprint","IMPRINT",FACE,{"disambiguationData":[TD([[makeQuery(id+"F0.imprint","IMPRINT",EDGE,{"disambiguationData":[TD([[subQ2,1.0]])],"derivedFrom":subQ1}),1.0]])]});}
            var Q2;
            {var subQ0=sQuery(id+"F0.wireOp",EDGE,"E19");var subQ1=sQuery(id+"F0.wireOp",EDGE,"E0");var subQ2=makeQuery(id+"F0.imprint","INTERSECT",VERTEX,{"disambiguationData":[OD(1.0)],"derivedFrom":[subQ1,subQ0]});Q2=makeQuery(id+"F0.imprint","IMPRINT",FACE,{"disambiguationData":[TD([[makeQuery(id+"F0.imprint","IMPRINT",EDGE,{"disambiguationData":[TD([[subQ2,1.0]])],"derivedFrom":subQ0}),1.0]])]});}
            var Q3;
            {var subQ0=sQuery(id+"F0.wireOp",EDGE,"E19");var subQ1=sQuery(id+"F0.wireOp",EDGE,"E0");var subQ2=makeQuery(id+"F0.imprint","INTERSECT",VERTEX,{"disambiguationData":[OD(0.0)],"derivedFrom":[subQ1,subQ0]});Q3=makeQuery(id+"F0.imprint","IMPRINT",FACE,{"disambiguationData":[TD([[makeQuery(id+"F0.imprint","IMPRINT",EDGE,{"disambiguationData":[TD([[subQ2,-1.0]])],"derivedFrom":subQ0}),1.0]])]});}
            var Q4;
            {var subQ0=sQuery(id+"F0.wireOp",EDGE,"E12");var subQ1=sQuery(id+"F0.wireOp",EDGE,"E1");var subQ2=makeQuery(id+"F0.imprint","INTERSECT",VERTEX,{"derivedFrom":[subQ1,subQ0]});Q4=makeQuery(id+"F0.imprint","IMPRINT",FACE,{"disambiguationData":[TD([[makeQuery(id+"F0.imprint","IMPRINT",EDGE,{"disambiguationData":[TD([[subQ2,-1.0]])],"derivedFrom":subQ1}),1.0]])]});}
            var Q5;
            {var subQ0=sQuery(id+"F0.wireOp",EDGE,"E12");var subQ1=sQuery(id+"F0.wireOp",EDGE,"E1");var subQ2=makeQuery(id+"F0.imprint","INTERSECT",VERTEX,{"derivedFrom":[subQ1,subQ0]});Q5=makeQuery(id+"F0.imprint","IMPRINT",FACE,{"disambiguationData":[TD([[makeQuery(id+"F0.imprint","IMPRINT",EDGE,{"disambiguationData":[TD([[subQ2,1.0]])],"derivedFrom":subQ1}),1.0]])]});}
            var Q6;
            {var subQ0=sQuery(id+"F0.wireOp",EDGE,"E19");var subQ1=sQuery(id+"F0.wireOp",EDGE,"E1");var subQ2=makeQuery(id+"F0.imprint","INTERSECT",VERTEX,{"disambiguationData":[OD(0.0)],"derivedFrom":[subQ1,subQ0]});Q6=makeQuery(id+"F0.imprint","IMPRINT",FACE,{"disambiguationData":[TD([[makeQuery(id+"F0.imprint","IMPRINT",EDGE,{"disambiguationData":[TD([[subQ2,-1.0]])],"derivedFrom":subQ0}),1.0]])]});}
            var Q7;
            {var subQ0=sQuery(id+"F0.wireOp",EDGE,"E19");var subQ1=sQuery(id+"F0.wireOp",EDGE,"E1");var subQ2=makeQuery(id+"F0.imprint","INTERSECT",VERTEX,{"disambiguationData":[OD(1.0)],"derivedFrom":[subQ1,subQ0]});Q7=makeQuery(id+"F0.imprint","IMPRINT",FACE,{"disambiguationData":[TD([[makeQuery(id+"F0.imprint","IMPRINT",EDGE,{"disambiguationData":[TD([[subQ2,1.0]])],"derivedFrom":subQ0}),1.0]])]});}
            var Q8;
            {var subQ0=sQuery(id+"F0.wireOp",EDGE,"E8");var subQ1=sQuery(id+"F0.wireOp",EDGE,"E2");var subQ2=makeQuery(id+"F0.imprint","INTERSECT",VERTEX,{"disambiguationData":[OD(1.0)],"derivedFrom":[subQ1,subQ0]});Q8=makeQuery(id+"F0.imprint","IMPRINT",FACE,{"disambiguationData":[TD([[makeQuery(id+"F0.imprint","IMPRINT",EDGE,{"disambiguationData":[TD([[subQ2,-1.0]])],"derivedFrom":subQ0}),1.0]])]});}
            var Q9;
            {var subQ0=sQuery(id+"F0.wireOp",EDGE,"E8");var subQ1=sQuery(id+"F0.wireOp",EDGE,"E2");var subQ2=makeQuery(id+"F0.imprint","INTERSECT",VERTEX,{"disambiguationData":[OD(0.0)],"derivedFrom":[subQ1,subQ0]});Q9=makeQuery(id+"F0.imprint","IMPRINT",FACE,{"disambiguationData":[TD([[makeQuery(id+"F0.imprint","IMPRINT",EDGE,{"disambiguationData":[TD([[subQ2,1.0]])],"derivedFrom":subQ0}),1.0]])]});}
            var Q10;
            {var subQ0=sQuery(id+"F0.wireOp",EDGE,"E8");var subQ1=sQuery(id+"F0.wireOp",EDGE,"E2");var subQ2=makeQuery(id+"F0.imprint","INTERSECT",VERTEX,{"disambiguationData":[OD(1.0)],"derivedFrom":[subQ1,subQ0]});Q10=makeQuery(id+"F0.imprint","IMPRINT",FACE,{"disambiguationData":[TD([[makeQuery(id+"F0.imprint","IMPRINT",EDGE,{"disambiguationData":[TD([[subQ2,-1.0]])],"derivedFrom":subQ0}),-1.0]])]});}
            var Q11;
            {var subQ0=sQuery(id+"F0.wireOp",EDGE,"E8");var subQ1=sQuery(id+"F0.wireOp",EDGE,"E2");var subQ2=makeQuery(id+"F0.imprint","INTERSECT",VERTEX,{"disambiguationData":[OD(0.0)],"derivedFrom":[subQ1,subQ0]});Q11=makeQuery(id+"F0.imprint","IMPRINT",FACE,{"disambiguationData":[TD([[makeQuery(id+"F0.imprint","IMPRINT",EDGE,{"disambiguationData":[TD([[subQ2,1.0]])],"derivedFrom":subQ0}),-1.0]])]});}
            var Q12;
            {var subQ0=sQuery(id+"F0.wireOp",EDGE,"E8");var subQ1=sQuery(id+"F0.wireOp",EDGE,"E3");var subQ2=makeQuery(id+"F0.imprint","INTERSECT",VERTEX,{"disambiguationData":[OD(1.0)],"derivedFrom":[subQ1,subQ0]});Q12=makeQuery(id+"F0.imprint","IMPRINT",FACE,{"disambiguationData":[TD([[makeQuery(id+"F0.imprint","IMPRINT",EDGE,{"disambiguationData":[TD([[subQ2,-1.0]])],"derivedFrom":subQ0}),1.0]])]});}
            var Q13;
            {var subQ0=sQuery(id+"F0.wireOp",EDGE,"E8");var subQ1=sQuery(id+"F0.wireOp",EDGE,"E3");var subQ2=makeQuery(id+"F0.imprint","INTERSECT",VERTEX,{"disambiguationData":[OD(1.0)],"derivedFrom":[subQ1,subQ0]});Q13=makeQuery(id+"F0.imprint","IMPRINT",FACE,{"disambiguationData":[TD([[makeQuery(id+"F0.imprint","IMPRINT",EDGE,{"disambiguationData":[TD([[subQ2,-1.0]])],"derivedFrom":subQ0}),-1.0]])]});}
            var Q14;
            {var subQ0=sQuery(id+"F0.wireOp",EDGE,"E8");var subQ1=sQuery(id+"F0.wireOp",EDGE,"E3");var subQ2=makeQuery(id+"F0.imprint","INTERSECT",VERTEX,{"disambiguationData":[OD(0.0)],"derivedFrom":[subQ1,subQ0]});Q14=makeQuery(id+"F0.imprint","IMPRINT",FACE,{"disambiguationData":[TD([[makeQuery(id+"F0.imprint","IMPRINT",EDGE,{"disambiguationData":[TD([[subQ2,1.0]])],"derivedFrom":subQ0}),-1.0]])]});}
            var Q15;
            {var subQ0=sQuery(id+"F0.wireOp",EDGE,"E8");var subQ1=sQuery(id+"F0.wireOp",EDGE,"E3");var subQ2=makeQuery(id+"F0.imprint","INTERSECT",VERTEX,{"disambiguationData":[OD(0.0)],"derivedFrom":[subQ1,subQ0]});Q15=makeQuery(id+"F0.imprint","IMPRINT",FACE,{"disambiguationData":[TD([[makeQuery(id+"F0.imprint","IMPRINT",EDGE,{"disambiguationData":[TD([[subQ2,1.0]])],"derivedFrom":subQ0}),1.0]])]});}
            var Q16;
            {var subQ0=sQuery(id+"F0.wireOp",EDGE,"E18");var subQ1=sQuery(id+"F0.wireOp",EDGE,"E4");var subQ2=makeQuery(id+"F0.imprint","INTERSECT",VERTEX,{"disambiguationData":[OD(0.0)],"derivedFrom":[subQ1,subQ0]});Q16=makeQuery(id+"F0.imprint","IMPRINT",FACE,{"disambiguationData":[TD([[makeQuery(id+"F0.imprint","IMPRINT",EDGE,{"disambiguationData":[TD([[subQ2,1.0]])],"derivedFrom":subQ0}),1.0]])]});}
            var Q17;
            {var subQ0=sQuery(id+"F0.wireOp",EDGE,"E18");var subQ1=sQuery(id+"F0.wireOp",EDGE,"E4");var subQ2=makeQuery(id+"F0.imprint","INTERSECT",VERTEX,{"disambiguationData":[OD(1.0)],"derivedFrom":[subQ1,subQ0]});Q17=makeQuery(id+"F0.imprint","IMPRINT",FACE,{"disambiguationData":[TD([[makeQuery(id+"F0.imprint","IMPRINT",EDGE,{"disambiguationData":[TD([[subQ2,-1.0]])],"derivedFrom":subQ0}),1.0]])]});}
            var Q18;
            {var subQ0=sQuery(id+"F0.wireOp",EDGE,"E18");var subQ1=sQuery(id+"F0.wireOp",EDGE,"E4");var subQ2=makeQuery(id+"F0.imprint","INTERSECT",VERTEX,{"disambiguationData":[OD(1.0)],"derivedFrom":[subQ1,subQ0]});Q18=makeQuery(id+"F0.imprint","IMPRINT",FACE,{"disambiguationData":[TD([[makeQuery(id+"F0.imprint","IMPRINT",EDGE,{"disambiguationData":[TD([[subQ2,-1.0]])],"derivedFrom":subQ1}),1.0]])]});}
            var Q19;
            {var subQ0=sQuery(id+"F0.wireOp",EDGE,"E18");var subQ1=sQuery(id+"F0.wireOp",EDGE,"E4");var subQ2=makeQuery(id+"F0.imprint","INTERSECT",VERTEX,{"disambiguationData":[OD(0.0)],"derivedFrom":[subQ1,subQ0]});Q19=makeQuery(id+"F0.imprint","IMPRINT",FACE,{"disambiguationData":[TD([[makeQuery(id+"F0.imprint","IMPRINT",EDGE,{"disambiguationData":[TD([[subQ2,1.0]])],"derivedFrom":subQ1}),1.0]])]});}
            var Q20;
            {var subQ0=sQuery(id+"F0.wireOp",EDGE,"E18");var subQ1=sQuery(id+"F0.wireOp",EDGE,"E5");var subQ2=makeQuery(id+"F0.imprint","INTERSECT",VERTEX,{"disambiguationData":[OD(1.0)],"derivedFrom":[subQ1,subQ0]});Q20=makeQuery(id+"F0.imprint","IMPRINT",FACE,{"disambiguationData":[TD([[makeQuery(id+"F0.imprint","IMPRINT",EDGE,{"disambiguationData":[TD([[subQ2,-1.0]])],"derivedFrom":subQ0}),1.0]])]});}
            var Q21;
            {var subQ0=sQuery(id+"F0.wireOp",EDGE,"E18");var subQ1=sQuery(id+"F0.wireOp",EDGE,"E5");var subQ2=makeQuery(id+"F0.imprint","INTERSECT",VERTEX,{"disambiguationData":[OD(1.0)],"derivedFrom":[subQ1,subQ0]});Q21=makeQuery(id+"F0.imprint","IMPRINT",FACE,{"disambiguationData":[TD([[makeQuery(id+"F0.imprint","IMPRINT",EDGE,{"disambiguationData":[TD([[subQ2,-1.0]])],"derivedFrom":subQ1}),1.0]])]});}
            var Q22;
            {var subQ0=sQuery(id+"F0.wireOp",EDGE,"E18");var subQ1=sQuery(id+"F0.wireOp",EDGE,"E5");var subQ2=makeQuery(id+"F0.imprint","INTERSECT",VERTEX,{"disambiguationData":[OD(0.0)],"derivedFrom":[subQ1,subQ0]});Q22=makeQuery(id+"F0.imprint","IMPRINT",FACE,{"disambiguationData":[TD([[makeQuery(id+"F0.imprint","IMPRINT",EDGE,{"disambiguationData":[TD([[subQ2,1.0]])],"derivedFrom":subQ1}),1.0]])]});}
            var Q23;
            {var subQ0=sQuery(id+"F0.wireOp",EDGE,"E18");var subQ1=sQuery(id+"F0.wireOp",EDGE,"E5");var subQ2=makeQuery(id+"F0.imprint","INTERSECT",VERTEX,{"disambiguationData":[OD(0.0)],"derivedFrom":[subQ1,subQ0]});Q23=makeQuery(id+"F0.imprint","IMPRINT",FACE,{"disambiguationData":[TD([[makeQuery(id+"F0.imprint","IMPRINT",EDGE,{"disambiguationData":[TD([[subQ2,1.0]])],"derivedFrom":subQ0}),1.0]])]});}
            var Q24;
            {var subQ0=sQuery(id+"F0.wireOp",EDGE,"E16");var subQ1=sQuery(id+"F0.wireOp",EDGE,"E12");var subQ2=makeQuery(id+"F0.imprint","INTERSECT",VERTEX,{"derivedFrom":[subQ1,subQ0]});Q24=makeQuery(id+"F0.imprint","IMPRINT",FACE,{"disambiguationData":[TD([[makeQuery(id+"F0.imprint","IMPRINT",EDGE,{"disambiguationData":[TD([[subQ2,-1.0]])],"derivedFrom":subQ1}),-1.0]])]});}
            var Q25;
            {var subQ0=sQuery(id+"F0.wireOp",EDGE,"E16");var subQ1=sQuery(id+"F0.wireOp",EDGE,"E12");var subQ2=makeQuery(id+"F0.imprint","INTERSECT",VERTEX,{"derivedFrom":[subQ1,subQ0]});Q25=makeQuery(id+"F0.imprint","IMPRINT",FACE,{"disambiguationData":[TD([[makeQuery(id+"F0.imprint","IMPRINT",EDGE,{"disambiguationData":[TD([[subQ2,-1.0]])],"derivedFrom":subQ1}),1.0]])]});}
            var Q26;
            {var subQ0=sQuery(id+"F0.wireOp",EDGE,"E16");var subQ1=sQuery(id+"F0.wireOp",EDGE,"E12");var subQ2=makeQuery(id+"F0.imprint","INTERSECT",VERTEX,{"derivedFrom":[subQ1,subQ0]});Q26=makeQuery(id+"F0.imprint","IMPRINT",FACE,{"disambiguationData":[TD([[makeQuery(id+"F0.imprint","IMPRINT",EDGE,{"disambiguationData":[TD([[subQ2,1.0]])],"derivedFrom":subQ1}),1.0]])]});}
            var Q27;
            {var subQ0=sQuery(id+"F0.wireOp",EDGE,"E16");var subQ1=sQuery(id+"F0.wireOp",EDGE,"E12");var subQ2=makeQuery(id+"F0.imprint","INTERSECT",VERTEX,{"derivedFrom":[subQ1,subQ0]});Q27=makeQuery(id+"F0.imprint","IMPRINT",FACE,{"disambiguationData":[TD([[makeQuery(id+"F0.imprint","IMPRINT",EDGE,{"disambiguationData":[TD([[subQ2,1.0]])],"derivedFrom":subQ1}),-1.0]])]});}
            var Q28;
            {var subQ0=sQuery(id+"F0.wireOp",EDGE,"E16");var subQ1=sQuery(id+"F0.wireOp",EDGE,"E10");var subQ2=makeQuery(id+"F0.imprint","INTERSECT",VERTEX,{"derivedFrom":[subQ1,subQ0]});Q28=makeQuery(id+"F0.imprint","IMPRINT",FACE,{"disambiguationData":[TD([[makeQuery(id+"F0.imprint","IMPRINT",EDGE,{"disambiguationData":[TD([[subQ2,1.0]])],"derivedFrom":subQ1}),1.0]])]});}
            var Q29;
            {var subQ0=sQuery(id+"F0.wireOp",EDGE,"E16");var subQ1=sQuery(id+"F0.wireOp",EDGE,"E10");var subQ2=makeQuery(id+"F0.imprint","INTERSECT",VERTEX,{"derivedFrom":[subQ1,subQ0]});Q29=makeQuery(id+"F0.imprint","IMPRINT",FACE,{"disambiguationData":[TD([[makeQuery(id+"F0.imprint","IMPRINT",EDGE,{"disambiguationData":[TD([[subQ2,-1.0]])],"derivedFrom":subQ1}),1.0]])]});}
            var Q30;
            {var subQ0=sQuery(id+"F0.wireOp",EDGE,"E16");var subQ1=sQuery(id+"F0.wireOp",EDGE,"E10");var subQ2=makeQuery(id+"F0.imprint","INTERSECT",VERTEX,{"derivedFrom":[subQ1,subQ0]});Q30=makeQuery(id+"F0.imprint","IMPRINT",FACE,{"disambiguationData":[TD([[makeQuery(id+"F0.imprint","IMPRINT",EDGE,{"disambiguationData":[TD([[subQ2,-1.0]])],"derivedFrom":subQ1}),-1.0]])]});}
            var Q31;
            {var subQ0=sQuery(id+"F0.wireOp",EDGE,"E16");var subQ1=sQuery(id+"F0.wireOp",EDGE,"E10");var subQ2=makeQuery(id+"F0.imprint","INTERSECT",VERTEX,{"derivedFrom":[subQ1,subQ0]});Q31=makeQuery(id+"F0.imprint","IMPRINT",FACE,{"disambiguationData":[TD([[makeQuery(id+"F0.imprint","IMPRINT",EDGE,{"disambiguationData":[TD([[subQ2,1.0]])],"derivedFrom":subQ1}),-1.0]])]});}
            var Q32;
            {var subQ0=sQuery(id+"F0.wireOp",EDGE,"E15");var subQ1=sQuery(id+"F0.wireOp",EDGE,"E10");var subQ2=makeQuery(id+"F0.imprint","INTERSECT",VERTEX,{"derivedFrom":[subQ1,subQ0]});Q32=makeQuery(id+"F0.imprint","IMPRINT",FACE,{"disambiguationData":[TD([[makeQuery(id+"F0.imprint","IMPRINT",EDGE,{"disambiguationData":[TD([[subQ2,1.0]])],"derivedFrom":subQ1}),-1.0]])]});}
            var Q33;
            {var subQ0=sQuery(id+"F0.wireOp",EDGE,"E15");var subQ1=sQuery(id+"F0.wireOp",EDGE,"E10");var subQ2=makeQuery(id+"F0.imprint","INTERSECT",VERTEX,{"derivedFrom":[subQ1,subQ0]});Q33=makeQuery(id+"F0.imprint","IMPRINT",FACE,{"disambiguationData":[TD([[makeQuery(id+"F0.imprint","IMPRINT",EDGE,{"disambiguationData":[TD([[subQ2,-1.0]])],"derivedFrom":subQ1}),-1.0]])]});}
            var Q34;
            {var subQ0=sQuery(id+"F0.wireOp",EDGE,"E15");var subQ1=sQuery(id+"F0.wireOp",EDGE,"E10");var subQ2=makeQuery(id+"F0.imprint","INTERSECT",VERTEX,{"derivedFrom":[subQ1,subQ0]});Q34=makeQuery(id+"F0.imprint","IMPRINT",FACE,{"disambiguationData":[TD([[makeQuery(id+"F0.imprint","IMPRINT",EDGE,{"disambiguationData":[TD([[subQ2,-1.0]])],"derivedFrom":subQ1}),1.0]])]});}
            var Q35;
            {var subQ0=sQuery(id+"F0.wireOp",EDGE,"E15");var subQ1=sQuery(id+"F0.wireOp",EDGE,"E10");var subQ2=makeQuery(id+"F0.imprint","INTERSECT",VERTEX,{"derivedFrom":[subQ1,subQ0]});Q35=makeQuery(id+"F0.imprint","IMPRINT",FACE,{"disambiguationData":[TD([[makeQuery(id+"F0.imprint","IMPRINT",EDGE,{"disambiguationData":[TD([[subQ2,1.0]])],"derivedFrom":subQ1}),1.0]])]});}
            var Q36;
            {var subQ0=sQuery(id+"F0.wireOp",EDGE,"E15");var subQ1=sQuery(id+"F0.wireOp",EDGE,"E12");var subQ2=makeQuery(id+"F0.imprint","INTERSECT",VERTEX,{"derivedFrom":[subQ1,subQ0]});Q36=makeQuery(id+"F0.imprint","IMPRINT",FACE,{"disambiguationData":[TD([[makeQuery(id+"F0.imprint","IMPRINT",EDGE,{"disambiguationData":[TD([[subQ2,1.0]])],"derivedFrom":subQ1}),-1.0]])]});}
            var Q37;
            {var subQ0=sQuery(id+"F0.wireOp",EDGE,"E15");var subQ1=sQuery(id+"F0.wireOp",EDGE,"E12");var subQ2=makeQuery(id+"F0.imprint","INTERSECT",VERTEX,{"derivedFrom":[subQ1,subQ0]});Q37=makeQuery(id+"F0.imprint","IMPRINT",FACE,{"disambiguationData":[TD([[makeQuery(id+"F0.imprint","IMPRINT",EDGE,{"disambiguationData":[TD([[subQ2,-1.0]])],"derivedFrom":subQ1}),-1.0]])]});}
            var Q38;
            {var subQ0=sQuery(id+"F0.wireOp",EDGE,"E15");var subQ1=sQuery(id+"F0.wireOp",EDGE,"E12");var subQ2=makeQuery(id+"F0.imprint","INTERSECT",VERTEX,{"derivedFrom":[subQ1,subQ0]});Q38=makeQuery(id+"F0.imprint","IMPRINT",FACE,{"disambiguationData":[TD([[makeQuery(id+"F0.imprint","IMPRINT",EDGE,{"disambiguationData":[TD([[subQ2,-1.0]])],"derivedFrom":subQ1}),1.0]])]});}
            var Q39;
            {var subQ0=sQuery(id+"F0.wireOp",EDGE,"E15");var subQ1=sQuery(id+"F0.wireOp",EDGE,"E12");var subQ2=makeQuery(id+"F0.imprint","INTERSECT",VERTEX,{"derivedFrom":[subQ1,subQ0]});Q39=makeQuery(id+"F0.imprint","IMPRINT",FACE,{"disambiguationData":[TD([[makeQuery(id+"F0.imprint","IMPRINT",EDGE,{"disambiguationData":[TD([[subQ2,1.0]])],"derivedFrom":subQ1}),1.0]])]});}
            var Q40;
            {var subQ0=sQuery(id+"F0.wireOp",EDGE,"E19");var subQ1=sQuery(id+"F0.wireOp",EDGE,"E7");var subQ2=makeQuery(id+"F0.imprint","INTERSECT",VERTEX,{"derivedFrom":[subQ1,subQ0]});Q40=makeQuery(id+"F0.imprint","IMPRINT",FACE,{"disambiguationData":[TD([[makeQuery(id+"F0.imprint","IMPRINT",EDGE,{"disambiguationData":[TD([[subQ2,1.0]])],"derivedFrom":subQ0}),1.0]])]});}
            var Q41;
            {var subQ0=sQuery(id+"F0.wireOp",EDGE,"E19");var subQ1=sQuery(id+"F0.wireOp",EDGE,"E7");var subQ2=makeQuery(id+"F0.imprint","INTERSECT",VERTEX,{"derivedFrom":[subQ1,subQ0]});Q41=makeQuery(id+"F0.imprint","IMPRINT",FACE,{"disambiguationData":[TD([[makeQuery(id+"F0.imprint","IMPRINT",EDGE,{"disambiguationData":[TD([[subQ2,-1.0]])],"derivedFrom":subQ0}),1.0]])]});}
            var Q42;
            {var subQ0=sQuery(id+"F0.wireOp",EDGE,"E19");var subQ1=sQuery(id+"F0.wireOp",EDGE,"E7");var subQ2=makeQuery(id+"F0.imprint","INTERSECT",VERTEX,{"derivedFrom":[subQ1,subQ0]});Q42=makeQuery(id+"F0.imprint","IMPRINT",FACE,{"disambiguationData":[TD([[makeQuery(id+"F0.imprint","IMPRINT",EDGE,{"disambiguationData":[TD([[subQ2,-1.0]])],"derivedFrom":subQ0}),-1.0]])]});}
            var Q43;
            {var subQ0=sQuery(id+"F0.wireOp",EDGE,"E19");var subQ1=sQuery(id+"F0.wireOp",EDGE,"E7");var subQ2=makeQuery(id+"F0.imprint","INTERSECT",VERTEX,{"derivedFrom":[subQ1,subQ0]});Q43=makeQuery(id+"F0.imprint","IMPRINT",FACE,{"disambiguationData":[TD([[makeQuery(id+"F0.imprint","IMPRINT",EDGE,{"disambiguationData":[TD([[subQ2,1.0]])],"derivedFrom":subQ0}),-1.0]])]});}
            var Q44;
            {var subQ1=sQuery(id+"F0.wireOp",EDGE,"E0");var subQ5=sQuery(id+"F0.wireOp",EDGE,"E10");var subQ10=makeQuery(id+"F0.imprint","INTERSECT",VERTEX,{"derivedFrom":[subQ1,subQ5]});Q44=makeQuery(id+"F0.imprint","IMPRINT",FACE,{"disambiguationData":[TD([[makeQuery(id+"F0.imprint","IMPRINT",EDGE,{"disambiguationData":[TD([[subQ10,1.0]])],"derivedFrom":subQ1}),-1.0]])]});}
            var Q45;
            {var subQ5=sQuery(id+"F0.wireOp",EDGE,"E19");var subQ6=sQuery(id+"F0.wireOp",EDGE,"E0");var subQ7=makeQuery(id+"F0.imprint","INTERSECT",VERTEX,{"disambiguationData":[OD(0.0)],"derivedFrom":[subQ6,subQ5]});Q45=makeQuery(id+"F0.imprint","IMPRINT",FACE,{"disambiguationData":[TD([[makeQuery(id+"F0.imprint","IMPRINT",EDGE,{"disambiguationData":[TD([[subQ7,1.0]])],"derivedFrom":subQ5}),1.0]])]});}
            var Q46;
            {var subQ1=sQuery(id+"F0.wireOp",EDGE,"E19");var subQ6=sQuery(id+"F0.wireOp",EDGE,"E1");var subQ9=makeQuery(id+"F0.imprint","INTERSECT",VERTEX,{"disambiguationData":[OD(1.0)],"derivedFrom":[subQ6,subQ1]});Q46=makeQuery(id+"F0.imprint","IMPRINT",FACE,{"disambiguationData":[TD([[makeQuery(id+"F0.imprint","IMPRINT",EDGE,{"disambiguationData":[TD([[subQ9,-1.0]])],"derivedFrom":subQ1}),1.0]])]});}
            var Q47;
            {var subQ1=sQuery(id+"F0.wireOp",EDGE,"E1");var subQ5=sQuery(id+"F0.wireOp",EDGE,"E12");var subQ8=makeQuery(id+"F0.imprint","INTERSECT",VERTEX,{"derivedFrom":[subQ1,subQ5]});Q47=makeQuery(id+"F0.imprint","IMPRINT",FACE,{"disambiguationData":[TD([[makeQuery(id+"F0.imprint","IMPRINT",EDGE,{"disambiguationData":[TD([[subQ8,-1.0]])],"derivedFrom":subQ1}),-1.0]])]});}
            var Q48;
            {var subQ1=sQuery(id+"F0.wireOp",EDGE,"E8");var subQ7=sQuery(id+"F0.wireOp",EDGE,"E2");var subQ8=makeQuery(id+"F0.imprint","INTERSECT",VERTEX,{"disambiguationData":[OD(0.0)],"derivedFrom":[subQ7,subQ1]});Q48=makeQuery(id+"F0.imprint","IMPRINT",FACE,{"disambiguationData":[TD([[makeQuery(id+"F0.imprint","IMPRINT",EDGE,{"disambiguationData":[TD([[subQ8,-1.0]])],"derivedFrom":subQ1}),1.0]])]});}
            var Q49;
            {var subQ5=sQuery(id+"F0.wireOp",EDGE,"E8");var subQ7=sQuery(id+"F0.wireOp",EDGE,"E3");var subQ8=makeQuery(id+"F0.imprint","INTERSECT",VERTEX,{"disambiguationData":[OD(1.0)],"derivedFrom":[subQ7,subQ5]});Q49=makeQuery(id+"F0.imprint","IMPRINT",FACE,{"disambiguationData":[TD([[makeQuery(id+"F0.imprint","IMPRINT",EDGE,{"disambiguationData":[TD([[subQ8,1.0]])],"derivedFrom":subQ5}),1.0]])]});}
            var Q50;
            {var subQ0=sQuery(id+"F0.wireOp",EDGE,"E8");var subQ1=sQuery(id+"F0.wireOp",EDGE,"E7");var subQ2=makeQuery(id+"F0.imprint","INTERSECT",VERTEX,{"derivedFrom":[subQ1,subQ0]});Q50=makeQuery(id+"F0.imprint","IMPRINT",FACE,{"disambiguationData":[TD([[makeQuery(id+"F0.imprint","IMPRINT",EDGE,{"disambiguationData":[TD([[subQ2,1.0]])],"derivedFrom":subQ0}),1.0]])]});}
            var Q51;
            {var subQ0=sQuery(id+"F0.wireOp",EDGE,"E8");var subQ1=sQuery(id+"F0.wireOp",EDGE,"E7");var subQ2=makeQuery(id+"F0.imprint","INTERSECT",VERTEX,{"derivedFrom":[subQ1,subQ0]});Q51=makeQuery(id+"F0.imprint","IMPRINT",FACE,{"disambiguationData":[TD([[makeQuery(id+"F0.imprint","IMPRINT",EDGE,{"disambiguationData":[TD([[subQ2,-1.0]])],"derivedFrom":subQ0}),-1.0]])]});}
            var Q52;
            {var subQ0=sQuery(id+"F0.wireOp",EDGE,"E8");var subQ1=sQuery(id+"F0.wireOp",EDGE,"E7");var subQ2=makeQuery(id+"F0.imprint","INTERSECT",VERTEX,{"derivedFrom":[subQ1,subQ0]});Q52=makeQuery(id+"F0.imprint","IMPRINT",FACE,{"disambiguationData":[TD([[makeQuery(id+"F0.imprint","IMPRINT",EDGE,{"disambiguationData":[TD([[subQ2,1.0]])],"derivedFrom":subQ0}),-1.0]])]});}
            var Q53;
            {var subQ0=sQuery(id+"F0.wireOp",EDGE,"E8");var subQ1=sQuery(id+"F0.wireOp",EDGE,"E7");var subQ2=makeQuery(id+"F0.imprint","INTERSECT",VERTEX,{"derivedFrom":[subQ1,subQ0]});Q53=makeQuery(id+"F0.imprint","IMPRINT",FACE,{"disambiguationData":[TD([[makeQuery(id+"F0.imprint","IMPRINT",EDGE,{"disambiguationData":[TD([[subQ2,-1.0]])],"derivedFrom":subQ0}),1.0]])]});}
            var Q54;
            {var subQ5=sQuery(id+"F0.wireOp",EDGE,"E8");var subQ7=sQuery(id+"F0.wireOp",EDGE,"E3");var subQ8=makeQuery(id+"F0.imprint","INTERSECT",VERTEX,{"disambiguationData":[OD(1.0)],"derivedFrom":[subQ7,subQ5]});Q54=makeQuery(id+"F0.imprint","IMPRINT",FACE,{"disambiguationData":[TD([[makeQuery(id+"F0.imprint","IMPRINT",EDGE,{"disambiguationData":[TD([[subQ8,1.0]])],"derivedFrom":subQ5}),-1.0]])]});}
            var Q55;
            {var subQ1=sQuery(id+"F0.wireOp",EDGE,"E8");var subQ7=sQuery(id+"F0.wireOp",EDGE,"E2");var subQ8=makeQuery(id+"F0.imprint","INTERSECT",VERTEX,{"disambiguationData":[OD(0.0)],"derivedFrom":[subQ7,subQ1]});Q55=makeQuery(id+"F0.imprint","IMPRINT",FACE,{"disambiguationData":[TD([[makeQuery(id+"F0.imprint","IMPRINT",EDGE,{"disambiguationData":[TD([[subQ8,-1.0]])],"derivedFrom":subQ1}),-1.0]])]});}
            var Q56;
            {var subQ1=sQuery(id+"F0.wireOp",EDGE,"E18");var subQ5=sQuery(id+"F0.wireOp",EDGE,"E4");var subQ6=makeQuery(id+"F0.imprint","INTERSECT",VERTEX,{"disambiguationData":[OD(0.0)],"derivedFrom":[subQ5,subQ1]});Q56=makeQuery(id+"F0.imprint","IMPRINT",FACE,{"disambiguationData":[TD([[makeQuery(id+"F0.imprint","IMPRINT",EDGE,{"disambiguationData":[TD([[subQ6,-1.0]])],"derivedFrom":subQ1}),1.0]])]});}
            var Q57;
            {var subQ3=sQuery(id+"F0.wireOp",EDGE,"E4");var subQ5=sQuery(id+"F0.wireOp",EDGE,"E18");var subQ6=makeQuery(id+"F0.imprint","INTERSECT",VERTEX,{"disambiguationData":[OD(0.0)],"derivedFrom":[subQ3,subQ5]});Q57=makeQuery(id+"F0.imprint","IMPRINT",FACE,{"disambiguationData":[TD([[makeQuery(id+"F0.imprint","IMPRINT",EDGE,{"disambiguationData":[TD([[subQ6,1.0]])],"derivedFrom":subQ3}),-1.0]])]});}
            var Q58;
            {var subQ0=sQuery(id+"F0.wireOp",EDGE,"E18");var subQ1=sQuery(id+"F0.wireOp",EDGE,"E7");var subQ2=makeQuery(id+"F0.imprint","INTERSECT",VERTEX,{"derivedFrom":[subQ1,subQ0]});Q58=makeQuery(id+"F0.imprint","IMPRINT",FACE,{"disambiguationData":[TD([[makeQuery(id+"F0.imprint","IMPRINT",EDGE,{"disambiguationData":[TD([[subQ2,1.0]])],"derivedFrom":subQ0}),-1.0]])]});}
            var Q59;
            {var subQ5=sQuery(id+"F0.wireOp",EDGE,"E18");var subQ6=sQuery(id+"F0.wireOp",EDGE,"E5");var subQ7=makeQuery(id+"F0.imprint","INTERSECT",VERTEX,{"disambiguationData":[OD(1.0)],"derivedFrom":[subQ6,subQ5]});Q59=makeQuery(id+"F0.imprint","IMPRINT",FACE,{"disambiguationData":[TD([[makeQuery(id+"F0.imprint","IMPRINT",EDGE,{"disambiguationData":[TD([[subQ7,-1.0]])],"derivedFrom":subQ6}),-1.0]])]});}
            var Q60;
            {var subQ0=sQuery(id+"F0.wireOp",EDGE,"E18");var subQ1=sQuery(id+"F0.wireOp",EDGE,"E7");var subQ2=makeQuery(id+"F0.imprint","INTERSECT",VERTEX,{"derivedFrom":[subQ1,subQ0]});Q60=makeQuery(id+"F0.imprint","IMPRINT",FACE,{"disambiguationData":[TD([[makeQuery(id+"F0.imprint","IMPRINT",EDGE,{"disambiguationData":[TD([[subQ2,-1.0]])],"derivedFrom":subQ0}),1.0]])]});}
            var Q61;
            {var subQ0=sQuery(id+"F0.wireOp",EDGE,"E18");var subQ1=sQuery(id+"F0.wireOp",EDGE,"E7");var subQ2=makeQuery(id+"F0.imprint","INTERSECT",VERTEX,{"derivedFrom":[subQ1,subQ0]});Q61=makeQuery(id+"F0.imprint","IMPRINT",FACE,{"disambiguationData":[TD([[makeQuery(id+"F0.imprint","IMPRINT",EDGE,{"disambiguationData":[TD([[subQ2,1.0]])],"derivedFrom":subQ0}),1.0]])]});}
            var Q62;
            {var subQ1=sQuery(id+"F0.wireOp",EDGE,"E5");var subQ5=sQuery(id+"F0.wireOp",EDGE,"E18");var subQ6=makeQuery(id+"F0.imprint","INTERSECT",VERTEX,{"disambiguationData":[OD(1.0)],"derivedFrom":[subQ1,subQ5]});Q62=makeQuery(id+"F0.imprint","IMPRINT",FACE,{"disambiguationData":[TD([[makeQuery(id+"F0.imprint","IMPRINT",EDGE,{"disambiguationData":[TD([[subQ6,1.0]])],"derivedFrom":subQ5}),1.0]])]});}
            var Q63;
            {var subQ0=sQuery(id+"F0.wireOp",EDGE,"E18");var subQ1=sQuery(id+"F0.wireOp",EDGE,"E7");var subQ2=makeQuery(id+"F0.imprint","INTERSECT",VERTEX,{"derivedFrom":[subQ1,subQ0]});Q63=makeQuery(id+"F0.imprint","IMPRINT",FACE,{"disambiguationData":[TD([[makeQuery(id+"F0.imprint","IMPRINT",EDGE,{"disambiguationData":[TD([[subQ2,-1.0]])],"derivedFrom":subQ0}),-1.0]])]});}
            var Q64;
            {var subQ0=sQuery(id+"F0.wireOp",EDGE,"E15");var subQ1=sQuery(id+"F0.wireOp",EDGE,"E7");var subQ2=makeQuery(id+"F0.imprint","INTERSECT",VERTEX,{"derivedFrom":[subQ1,subQ0]});Q64=makeQuery(id+"F0.imprint","IMPRINT",FACE,{"disambiguationData":[TD([[makeQuery(id+"F0.imprint","IMPRINT",EDGE,{"disambiguationData":[TD([[subQ2,-1.0]])],"derivedFrom":subQ1}),-1.0]])]});}
            var Q65;
            {var subQ0=sQuery(id+"F0.wireOp",EDGE,"E15");var subQ1=sQuery(id+"F0.wireOp",EDGE,"E7");var subQ2=makeQuery(id+"F0.imprint","INTERSECT",VERTEX,{"derivedFrom":[subQ1,subQ0]});Q65=makeQuery(id+"F0.imprint","IMPRINT",FACE,{"disambiguationData":[TD([[makeQuery(id+"F0.imprint","IMPRINT",EDGE,{"disambiguationData":[TD([[subQ2,-1.0]])],"derivedFrom":subQ1}),1.0]])]});}
            var Q66;
            {var subQ0=sQuery(id+"F0.wireOp",EDGE,"E15");var subQ1=sQuery(id+"F0.wireOp",EDGE,"E7");var subQ2=makeQuery(id+"F0.imprint","INTERSECT",VERTEX,{"derivedFrom":[subQ1,subQ0]});Q66=makeQuery(id+"F0.imprint","IMPRINT",FACE,{"disambiguationData":[TD([[makeQuery(id+"F0.imprint","IMPRINT",EDGE,{"disambiguationData":[TD([[subQ2,1.0]])],"derivedFrom":subQ1}),-1.0]])]});}
            var Q67;
            {var subQ0=sQuery(id+"F0.wireOp",EDGE,"E16");var subQ1=sQuery(id+"F0.wireOp",EDGE,"E7");var subQ2=makeQuery(id+"F0.imprint","INTERSECT",VERTEX,{"derivedFrom":[subQ1,subQ0]});Q67=makeQuery(id+"F0.imprint","IMPRINT",FACE,{"disambiguationData":[TD([[makeQuery(id+"F0.imprint","IMPRINT",EDGE,{"disambiguationData":[TD([[subQ2,1.0]])],"derivedFrom":subQ1}),-1.0]])]});}
            var Q68;
            {var subQ0=sQuery(id+"F0.wireOp",EDGE,"E16");var subQ1=sQuery(id+"F0.wireOp",EDGE,"E7");var subQ2=makeQuery(id+"F0.imprint","INTERSECT",VERTEX,{"derivedFrom":[subQ1,subQ0]});Q68=makeQuery(id+"F0.imprint","IMPRINT",FACE,{"disambiguationData":[TD([[makeQuery(id+"F0.imprint","IMPRINT",EDGE,{"disambiguationData":[TD([[subQ2,1.0]])],"derivedFrom":subQ1}),1.0]])]});}
            var Q69;
            {var subQ0=sQuery(id+"F0.wireOp",EDGE,"E16");var subQ1=sQuery(id+"F0.wireOp",EDGE,"E7");var subQ2=makeQuery(id+"F0.imprint","INTERSECT",VERTEX,{"derivedFrom":[subQ1,subQ0]});Q69=makeQuery(id+"F0.imprint","IMPRINT",FACE,{"disambiguationData":[TD([[makeQuery(id+"F0.imprint","IMPRINT",EDGE,{"disambiguationData":[TD([[subQ2,-1.0]])],"derivedFrom":subQ1}),-1.0]])]});}
            var Q70;
            {var subQ0=sQuery(id+"F0.wireOp",EDGE,"E16");var subQ1=sQuery(id+"F0.wireOp",EDGE,"E7");var subQ2=makeQuery(id+"F0.imprint","INTERSECT",VERTEX,{"derivedFrom":[subQ1,subQ0]});Q70=makeQuery(id+"F0.imprint","IMPRINT",FACE,{"disambiguationData":[TD([[makeQuery(id+"F0.imprint","IMPRINT",EDGE,{"disambiguationData":[TD([[subQ2,-1.0]])],"derivedFrom":subQ1}),1.0]])]});}
            var Q71;
            {var subQ0=sQuery(id+"F0.wireOp",EDGE,"E15");var subQ1=sQuery(id+"F0.wireOp",EDGE,"E7");var subQ2=makeQuery(id+"F0.imprint","INTERSECT",VERTEX,{"derivedFrom":[subQ1,subQ0]});Q71=makeQuery(id+"F0.imprint","IMPRINT",FACE,{"disambiguationData":[TD([[makeQuery(id+"F0.imprint","IMPRINT",EDGE,{"disambiguationData":[TD([[subQ2,1.0]])],"derivedFrom":subQ1}),1.0]])]});}
            var Q72;
            {var subQ1=sQuery(id+"F0.wireOp",EDGE,"E6.right");var subQ5=sQuery(id+"F0.wireOp",EDGE,"E8");var subQ6=makeQuery(id+"F0.imprint","INTERSECT",VERTEX,{"derivedFrom":[subQ1,subQ5]});Q72=makeQuery(id+"F0.imprint","IMPRINT",FACE,{"disambiguationData":[TD([[makeQuery(id+"F0.imprint","IMPRINT",EDGE,{"disambiguationData":[TD([[subQ6,1.0]])],"derivedFrom":subQ1}),1.0]])]});}
            var Q73;
            {var subQ0=sQuery(id+"F0.wireOp",EDGE,"E8");var subQ1=sQuery(id+"F0.wireOp",EDGE,"E6.right");var subQ2=makeQuery(id+"F0.imprint","INTERSECT",VERTEX,{"derivedFrom":[subQ1,subQ0]});Q73=makeQuery(id+"F0.imprint","IMPRINT",FACE,{"disambiguationData":[TD([[makeQuery(id+"F0.imprint","IMPRINT",EDGE,{"disambiguationData":[TD([[subQ2,-1.0]])],"derivedFrom":subQ1}),1.0]])]});}
            var Q74;
            {var subQ5=sQuery(id+"F0.wireOp",EDGE,"E19");var subQ6=sQuery(id+"F0.wireOp",EDGE,"E6.right");var subQ7=makeQuery(id+"F0.imprint","INTERSECT",VERTEX,{"derivedFrom":[subQ6,subQ5]});Q74=makeQuery(id+"F0.imprint","IMPRINT",FACE,{"disambiguationData":[TD([[makeQuery(id+"F0.imprint","IMPRINT",EDGE,{"disambiguationData":[TD([[subQ7,-1.0]])],"derivedFrom":subQ6}),1.0]])]});}
            var Q75;
            {var subQ0=sQuery(id+"F0.wireOp",EDGE,"E10");var subQ3=sQuery(id+"F0.wireOp",EDGE,"E0");var subQ4=makeQuery(id+"F0.imprint","INTERSECT",VERTEX,{"derivedFrom":[subQ3,subQ0]});Q75=makeQuery(id+"F0.imprint","IMPRINT",FACE,{"disambiguationData":[TD([[makeQuery(id+"F0.imprint","IMPRINT",EDGE,{"disambiguationData":[TD([[subQ4,-1.0]])],"derivedFrom":subQ3}),-1.0]])]});}
            var Q76;
            {var subQ0=sQuery(id+"F0.wireOp",EDGE,"E12");var subQ3=sQuery(id+"F0.wireOp",EDGE,"E1");var subQ4=makeQuery(id+"F0.imprint","INTERSECT",VERTEX,{"derivedFrom":[subQ3,subQ0]});Q76=makeQuery(id+"F0.imprint","IMPRINT",FACE,{"disambiguationData":[TD([[makeQuery(id+"F0.imprint","IMPRINT",EDGE,{"disambiguationData":[TD([[subQ4,1.0]])],"derivedFrom":subQ3}),-1.0]])]});}
            var Q77;
            {var subQ5=sQuery(id+"F0.wireOp",EDGE,"E19");var subQ6=sQuery(id+"F0.wireOp",EDGE,"E13");var subQ7=makeQuery(id+"F0.imprint","INTERSECT",VERTEX,{"derivedFrom":[subQ6,subQ5]});Q77=makeQuery(id+"F0.imprint","IMPRINT",FACE,{"disambiguationData":[TD([[makeQuery(id+"F0.imprint","IMPRINT",EDGE,{"disambiguationData":[TD([[subQ7,-1.0]])],"derivedFrom":subQ6}),-1.0]])]});}
            var Q78;
            {var subQ0=sQuery(id+"F0.wireOp",EDGE,"E14");var subQ1=sQuery(id+"F0.wireOp",EDGE,"E8");var subQ2=makeQuery(id+"F0.imprint","INTERSECT",VERTEX,{"derivedFrom":[subQ1,subQ0]});Q78=makeQuery(id+"F0.imprint","IMPRINT",FACE,{"disambiguationData":[TD([[makeQuery(id+"F0.imprint","IMPRINT",EDGE,{"disambiguationData":[TD([[subQ2,1.0]])],"derivedFrom":subQ1}),1.0]])]});}
            var Q79;
            {var subQ1=sQuery(id+"F0.wireOp",EDGE,"E14");var subQ5=sQuery(id+"F0.wireOp",EDGE,"E8");var subQ6=makeQuery(id+"F0.imprint","INTERSECT",VERTEX,{"derivedFrom":[subQ5,subQ1]});Q79=makeQuery(id+"F0.imprint","IMPRINT",FACE,{"disambiguationData":[TD([[makeQuery(id+"F0.imprint","IMPRINT",EDGE,{"disambiguationData":[TD([[subQ6,1.0]])],"derivedFrom":subQ5}),-1.0]])]});}
            var Q80;
            {var subQ0=sQuery(id+"F0.wireOp",EDGE,"E18");var subQ1=sQuery(id+"F0.wireOp",EDGE,"E6.left");var subQ2=makeQuery(id+"F0.imprint","INTERSECT",VERTEX,{"derivedFrom":[subQ1,subQ0]});Q80=makeQuery(id+"F0.imprint","IMPRINT",FACE,{"disambiguationData":[TD([[makeQuery(id+"F0.imprint","IMPRINT",EDGE,{"disambiguationData":[TD([[subQ2,1.0]])],"derivedFrom":subQ1}),-1.0]])]});}
            var Q81;
            {var subQ3=sQuery(id+"F0.wireOp",EDGE,"E5");var subQ9=sQuery(id+"F0.wireOp",EDGE,"E18");var subQ11=makeQuery(id+"F0.imprint","INTERSECT",VERTEX,{"disambiguationData":[OD(0.0)],"derivedFrom":[subQ3,subQ9]});Q81=makeQuery(id+"F0.imprint","IMPRINT",FACE,{"disambiguationData":[TD([[makeQuery(id+"F0.imprint","IMPRINT",EDGE,{"disambiguationData":[TD([[subQ11,1.0]])],"derivedFrom":subQ3}),-1.0]])]});}
            var Q82;
            {var subQ0=sQuery(id+"F0.wireOp",EDGE,"E18");var subQ8=sQuery(id+"F0.wireOp",EDGE,"E4");var subQ11=makeQuery(id+"F0.imprint","INTERSECT",VERTEX,{"disambiguationData":[OD(1.0)],"derivedFrom":[subQ8,subQ0]});Q82=makeQuery(id+"F0.imprint","IMPRINT",FACE,{"disambiguationData":[TD([[makeQuery(id+"F0.imprint","IMPRINT",EDGE,{"disambiguationData":[TD([[subQ11,-1.0]])],"derivedFrom":subQ8}),-1.0]])]});}
            var Q83;
            {var subQ0=sQuery(id+"F0.wireOp",EDGE,"E18");var subQ1=sQuery(id+"F0.wireOp",EDGE,"E17");var subQ2=makeQuery(id+"F0.imprint","INTERSECT",VERTEX,{"derivedFrom":[subQ1,subQ0]});Q83=makeQuery(id+"F0.imprint","IMPRINT",FACE,{"disambiguationData":[TD([[makeQuery(id+"F0.imprint","IMPRINT",EDGE,{"disambiguationData":[TD([[subQ2,1.0]])],"derivedFrom":subQ1}),1.0]])]});}
            extrude(context, id + "F2", {"entities" : qUnion([Q0, Q1, Q2, Q3, Q4, Q5, Q6, Q7, Q8, Q9, Q10, Q11, Q12, Q13, Q14, Q15, Q16, Q17, Q18, Q19, Q20, Q21, Q22, Q23, Q24, Q25, Q26, Q27, Q28, Q29, Q30, Q31, Q32, Q33, Q34, Q35, Q36, Q37, Q38, Q39, Q40, Q41, Q42, Q43, Q44, Q45, Q46, Q47, Q48, Q49, Q50, Q51, Q52, Q53, Q54, Q55, Q56, Q57, Q58, Q59, Q60, Q61, Q62, Q63, Q64, Q65, Q66, Q67, Q68, Q69, Q70, Q71, Q72, Q73, Q74, Q75, Q76, Q77, Q78, Q79, Q80, Q81, Q82, Q83]), "endBound" : BoundingType.SYMMETRIC, "oppositeDirection" : true, "depth" : 2.54 * mm});
        }
        {
            var Q0;
            Q0=qCreatedBy(makeId("Right.planeOp"),FACE);
            var sketch = newSketch(context, id + "F3", { "sketchPlane" : qUnion([Q0])});
            skLineSegment(sketch, "E26", {"start": v(0, 0) * mm, "end": v(50.8, 0) * mm});
            skLineSegment(sketch, "E27", {"start": v(50.8, 0) * mm, "end": v(50.8, 25.4) * mm});
            skLineSegment(sketch, "E28", {"start": v(0, 0) * mm, "end": v(0, 50.8) * mm});
            skLineSegment(sketch, "E29", {"start": v(0, 50.8) * mm, "end": v(25.4, 50.8) * mm});
            skLineSegment(sketch, "E30", {"start": v(25.4, 50.8) * mm, "end": v(50.8, 25.4) * mm});
            skLineSegment(sketch, "E31", {"start": v(0, 50.8) * mm, "end": v(-25.4, 50.8) * mm});
            skLineSegment(sketch, "E32", {"start": v(0, 0) * mm, "end": v(-50.8, 0) * mm});
            skLineSegment(sketch, "E33", {"start": v(-50.8, 0) * mm, "end": v(-50.8, 25.4) * mm});
            skLineSegment(sketch, "E34", {"start": v(-50.8, 25.4) * mm, "end": v(-25.4, 50.8) * mm});
            skLineSegment(sketch, "E35", {"start": v(0, 50.8) * mm, "end": v(0, 41.61) * mm});
            skLineSegment(sketch, "E36", {"start": v(0, 41.61) * mm, "end": v(25.4, 41.61) * mm});
            skLineSegment(sketch, "E37", {"start": v(25.4, 41.61) * mm, "end": v(50.8, 16.21) * mm});
            skLineSegment(sketch, "E38", {"start": v(0, 41.61) * mm, "end": v(-25.4, 41.61) * mm});
            skLineSegment(sketch, "E39", {"start": v(-25.4, 41.61) * mm, "end": v(-50.8, 16.21) * mm});
            skSolve(sketch);
        }
        {
            var Q0;
            Q0=makeQuery(id+"F3.imprint","IMPRINT",FACE,{"disambiguationData":[TD([[makeQuery(id+"F3.imprint","IMPRINT",EDGE,{"derivedFrom":sQuery(id+"F3.wireOp",EDGE,"E29")}),-1.0]])]});
            var Q1;
            Q1=makeQuery(id+"F3.imprint","IMPRINT",FACE,{"disambiguationData":[TD([[makeQuery(id+"F3.imprint","IMPRINT",EDGE,{"derivedFrom":sQuery(id+"F3.wireOp",EDGE,"E31")}),1.0]])]});
            extrude(context, id + "F4", {"entities" : qUnion([Q0, Q1]), "operationType" : NewBodyOperationType.ADD, "endBound" : BoundingType.SYMMETRIC, "depth" : 12.7 * mm});
        }
    });
